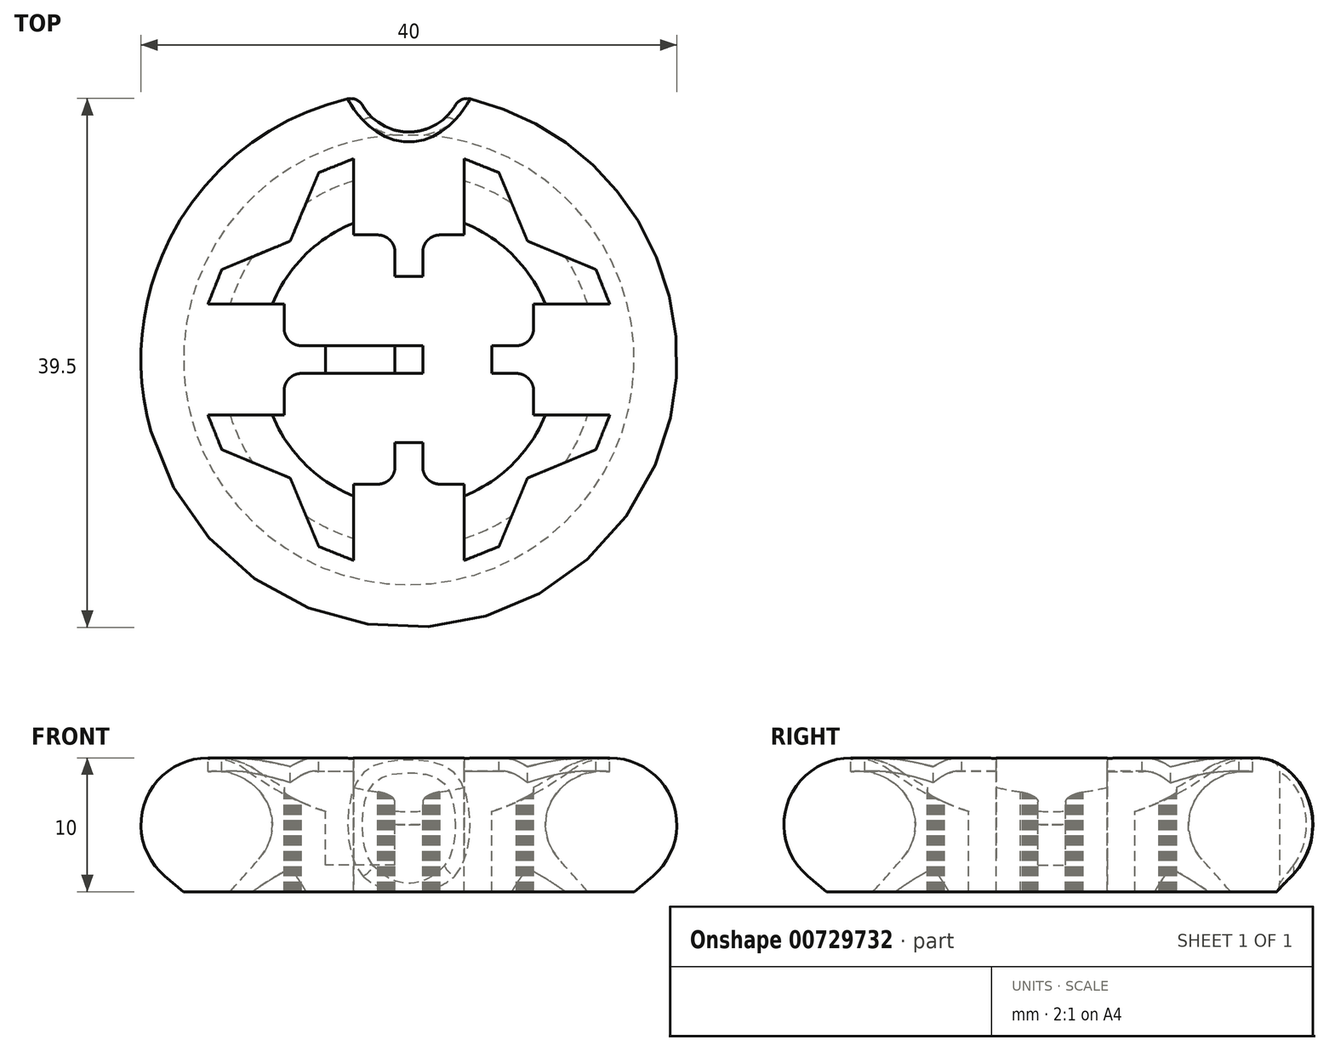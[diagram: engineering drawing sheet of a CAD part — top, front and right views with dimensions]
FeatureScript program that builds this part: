
annotation { "Feature Type Name" : "Feature", "Feature Type Description" : "" }
export const myFeature = defineFeature(function(context is Context, id is Id, definition is map)
    precondition{}
    {
        {
            var Q0;
            Q0=qCreatedBy(makeId("Front.planeOp"),FACE);
            var sketch = newSketch(context, id + "F0", { "sketchPlane" : qUnion([Q0])});
            skArc(sketch, "E0", {"start": v(-12, 9) * mm, "mid": v(-6.32, 6.03) * mm, "end": v(0, 5) * mm});
            skArc(sketch, "E1", {"start": v(-12, 9) * mm, "mid": v(-19.74, 6.58) * mm, "end": v(-15, 0) * mm});
            skLineSegment(sketch, "E2", {"start": v(0, 0) * mm, "end": v(-15, 0) * mm});
            skLineSegment(sketch, "E3", {"start": v(0, 0) * mm, "end": v(0, 5) * mm});
            skLineSegment(sketch, "E4", {"start": v(-18.21, 1.17) * mm, "end": v(-16.82, 0) * mm});
            skLineSegment(sketch, "E5", {"start": v(-16.82, 0) * mm, "end": v(-15, 0) * mm});
            skSolve(sketch);
        }
        {
            var Q0;
            Q0 = qSketchRegion(id + "F0", true);
            var Q1;
            Q1=sQuery(id+"F0.wireOp",EDGE,"E3");
            revolve(context, id + "F1", {"surfaceOperationType" : NewSurfaceOperationType.NEW, "entities" : qUnion([Q0]), "axis" : qUnion([Q1]), "revolveType" : RevolveType.FULL});
        }
        {
            var Q0;
            Q0=qCreatedBy(makeId("Top.planeOp"),FACE);
            cPlane(context, id + "F2", {"entities" : qUnion([Q0]), "cplaneType" : CPlaneType.OFFSET, "offset" : 15 * mm, "width" : 150 * mm, "height" : 150 * mm});
        }
        {
            var Q0;
            Q0=qCreatedBy(id+"F2.planeOp",FACE);
            var sketch = newSketch(context, id + "F3", { "sketchPlane" : qUnion([Q0])});
            skLineSegment(sketch, "E6", {"start": v(9.31, -4.14) * mm, "end": v(9.31, -4.02) * mm});
            skLineSegment(sketch, "E7", {"start": v(9.31, -4.02) * mm, "end": v(9.31, -3.91) * mm});
            skLineSegment(sketch, "E8", {"start": v(9.31, -3.91) * mm, "end": v(9.31, -3.8) * mm});
            skLineSegment(sketch, "E9", {"start": v(9.31, -3.8) * mm, "end": v(9.31, -3.69) * mm});
            skLineSegment(sketch, "E10", {"start": v(9.31, -3.69) * mm, "end": v(9.31, -3.57) * mm});
            skLineSegment(sketch, "E11", {"start": v(9.31, -3.57) * mm, "end": v(9.31, -3.46) * mm});
            skLineSegment(sketch, "E12", {"start": v(9.31, -3.46) * mm, "end": v(9.31, -3.35) * mm});
            skLineSegment(sketch, "E13", {"start": v(9.31, -3.35) * mm, "end": v(9.31, -3.23) * mm});
            skLineSegment(sketch, "E14", {"start": v(9.31, -3.23) * mm, "end": v(9.31, -3.12) * mm});
            skLineSegment(sketch, "E15", {"start": v(9.31, -3.12) * mm, "end": v(9.31, -3) * mm});
            skLineSegment(sketch, "E16", {"start": v(9.31, -3) * mm, "end": v(9.31, -2.9) * mm});
            skLineSegment(sketch, "E17", {"start": v(9.31, -2.9) * mm, "end": v(9.31, -2.78) * mm});
            skLineSegment(sketch, "E18", {"start": v(9.31, -2.78) * mm, "end": v(9.31, -2.67) * mm});
            skLineSegment(sketch, "E19", {"start": v(9.31, -2.67) * mm, "end": v(9.31, -2.55) * mm});
            skLineSegment(sketch, "E20", {"start": v(9.31, -2.55) * mm, "end": v(9.31, -2.44) * mm});
            skLineSegment(sketch, "E21", {"start": v(9.31, -2.44) * mm, "end": v(9.31, -2.33) * mm});
            skLineSegment(sketch, "E22", {"start": v(9.31, -2.33) * mm, "end": v(9.3, -2.2) * mm});
            skLineSegment(sketch, "E23", {"start": v(9.3, -2.2) * mm, "end": v(9.28, -2.07) * mm});
            skLineSegment(sketch, "E24", {"start": v(9.28, -2.07) * mm, "end": v(9.25, -1.94) * mm});
            skLineSegment(sketch, "E25", {"start": v(9.25, -1.94) * mm, "end": v(9.2, -1.82) * mm});
            skLineSegment(sketch, "E26", {"start": v(9.2, -1.82) * mm, "end": v(9.15, -1.71) * mm});
            skLineSegment(sketch, "E27", {"start": v(9.15, -1.71) * mm, "end": v(9.09, -1.6) * mm});
            skLineSegment(sketch, "E28", {"start": v(9.09, -1.6) * mm, "end": v(9.02, -1.5) * mm});
            skLineSegment(sketch, "E29", {"start": v(9.02, -1.5) * mm, "end": v(8.93, -1.41) * mm});
            skLineSegment(sketch, "E30", {"start": v(8.93, -1.41) * mm, "end": v(8.84, -1.33) * mm});
            skLineSegment(sketch, "E31", {"start": v(8.84, -1.33) * mm, "end": v(8.74, -1.26) * mm});
            skLineSegment(sketch, "E32", {"start": v(8.74, -1.26) * mm, "end": v(8.63, -1.2) * mm});
            skLineSegment(sketch, "E33", {"start": v(8.63, -1.2) * mm, "end": v(8.52, -1.14) * mm});
            skLineSegment(sketch, "E34", {"start": v(8.52, -1.14) * mm, "end": v(8.4, -1.1) * mm});
            skLineSegment(sketch, "E35", {"start": v(8.4, -1.1) * mm, "end": v(8.28, -1.06) * mm});
            skLineSegment(sketch, "E36", {"start": v(8.28, -1.06) * mm, "end": v(8.15, -1.04) * mm});
            skLineSegment(sketch, "E37", {"start": v(8.15, -1.04) * mm, "end": v(8.02, -1.03) * mm});
            skLineSegment(sketch, "E38", {"start": v(8.02, -1.03) * mm, "end": v(7.9, -1.03) * mm});
            skLineSegment(sketch, "E39", {"start": v(7.9, -1.03) * mm, "end": v(7.8, -1.03) * mm});
            skLineSegment(sketch, "E40", {"start": v(7.8, -1.03) * mm, "end": v(7.68, -1.03) * mm});
            skLineSegment(sketch, "E41", {"start": v(7.68, -1.03) * mm, "end": v(7.56, -1.03) * mm});
            skLineSegment(sketch, "E42", {"start": v(7.56, -1.03) * mm, "end": v(7.45, -1.03) * mm});
            skLineSegment(sketch, "E43", {"start": v(7.45, -1.03) * mm, "end": v(7.34, -1.03) * mm});
            skLineSegment(sketch, "E44", {"start": v(7.34, -1.03) * mm, "end": v(7.23, -1.03) * mm});
            skLineSegment(sketch, "E45", {"start": v(7.23, -1.03) * mm, "end": v(7.11, -1.03) * mm});
            skLineSegment(sketch, "E46", {"start": v(7.11, -1.03) * mm, "end": v(7, -1.03) * mm});
            skLineSegment(sketch, "E47", {"start": v(7, -1.03) * mm, "end": v(6.89, -1.03) * mm});
            skLineSegment(sketch, "E48", {"start": v(6.89, -1.03) * mm, "end": v(6.77, -1.03) * mm});
            skLineSegment(sketch, "E49", {"start": v(6.77, -1.03) * mm, "end": v(6.66, -1.03) * mm});
            skLineSegment(sketch, "E50", {"start": v(6.66, -1.03) * mm, "end": v(6.55, -1.03) * mm});
            skLineSegment(sketch, "E51", {"start": v(6.55, -1.03) * mm, "end": v(6.43, -1.03) * mm});
            skLineSegment(sketch, "E52", {"start": v(6.43, -1.03) * mm, "end": v(6.32, -1.03) * mm});
            skLineSegment(sketch, "E53", {"start": v(6.32, -1.03) * mm, "end": v(6.2, -1.03) * mm});
            skLineSegment(sketch, "E54", {"start": v(6.2, -1.03) * mm, "end": v(6.2, -0.97) * mm});
            skLineSegment(sketch, "E55", {"start": v(6.2, -0.97) * mm, "end": v(6.2, -0.9) * mm});
            skLineSegment(sketch, "E56", {"start": v(6.2, -0.9) * mm, "end": v(6.2, -0.84) * mm});
            skLineSegment(sketch, "E57", {"start": v(6.2, -0.84) * mm, "end": v(6.2, -0.78) * mm});
            skLineSegment(sketch, "E58", {"start": v(6.2, -0.78) * mm, "end": v(6.2, -0.71) * mm});
            skLineSegment(sketch, "E59", {"start": v(6.2, -0.71) * mm, "end": v(6.2, -0.65) * mm});
            skLineSegment(sketch, "E60", {"start": v(6.2, -0.65) * mm, "end": v(6.2, -0.58) * mm});
            skLineSegment(sketch, "E61", {"start": v(6.2, -0.58) * mm, "end": v(6.2, -0.52) * mm});
            skLineSegment(sketch, "E62", {"start": v(6.2, -0.52) * mm, "end": v(6.2, -0.45) * mm});
            skLineSegment(sketch, "E63", {"start": v(6.2, -0.45) * mm, "end": v(6.2, -0.39) * mm});
            skLineSegment(sketch, "E64", {"start": v(6.2, -0.39) * mm, "end": v(6.2, -0.32) * mm});
            skLineSegment(sketch, "E65", {"start": v(6.2, -0.32) * mm, "end": v(6.2, -0.26) * mm});
            skLineSegment(sketch, "E66", {"start": v(6.2, -0.26) * mm, "end": v(6.2, -0.2) * mm});
            skLineSegment(sketch, "E67", {"start": v(6.2, -0.2) * mm, "end": v(6.2, -0.13) * mm});
            skLineSegment(sketch, "E68", {"start": v(6.2, -0.13) * mm, "end": v(6.2, -0.06) * mm});
            skLineSegment(sketch, "E69", {"start": v(6.2, -0.06) * mm, "end": v(6.2, 0) * mm});
            skLineSegment(sketch, "E70", {"start": v(6.2, 0) * mm, "end": v(6.2, 0.06) * mm});
            skLineSegment(sketch, "E71", {"start": v(6.2, 0.06) * mm, "end": v(6.2, 0.13) * mm});
            skLineSegment(sketch, "E72", {"start": v(6.2, 0.13) * mm, "end": v(6.2, 0.2) * mm});
            skLineSegment(sketch, "E73", {"start": v(6.2, 0.2) * mm, "end": v(6.2, 0.26) * mm});
            skLineSegment(sketch, "E74", {"start": v(6.2, 0.26) * mm, "end": v(6.2, 0.32) * mm});
            skLineSegment(sketch, "E75", {"start": v(6.2, 0.32) * mm, "end": v(6.2, 0.39) * mm});
            skLineSegment(sketch, "E76", {"start": v(6.2, 0.39) * mm, "end": v(6.2, 0.45) * mm});
            skLineSegment(sketch, "E77", {"start": v(6.2, 0.45) * mm, "end": v(6.2, 0.52) * mm});
            skLineSegment(sketch, "E78", {"start": v(6.2, 0.52) * mm, "end": v(6.2, 0.58) * mm});
            skLineSegment(sketch, "E79", {"start": v(6.2, 0.58) * mm, "end": v(6.2, 0.65) * mm});
            skLineSegment(sketch, "E80", {"start": v(6.2, 0.65) * mm, "end": v(6.2, 0.71) * mm});
            skLineSegment(sketch, "E81", {"start": v(6.2, 0.71) * mm, "end": v(6.2, 0.78) * mm});
            skLineSegment(sketch, "E82", {"start": v(6.2, 0.78) * mm, "end": v(6.2, 0.84) * mm});
            skLineSegment(sketch, "E83", {"start": v(6.2, 0.84) * mm, "end": v(6.2, 0.9) * mm});
            skLineSegment(sketch, "E84", {"start": v(6.2, 0.9) * mm, "end": v(6.2, 0.97) * mm});
            skLineSegment(sketch, "E85", {"start": v(6.2, 0.97) * mm, "end": v(6.2, 1.03) * mm});
            skLineSegment(sketch, "E86", {"start": v(6.2, 1.03) * mm, "end": v(6.32, 1.03) * mm});
            skLineSegment(sketch, "E87", {"start": v(6.32, 1.03) * mm, "end": v(6.43, 1.03) * mm});
            skLineSegment(sketch, "E88", {"start": v(6.43, 1.03) * mm, "end": v(6.55, 1.03) * mm});
            skLineSegment(sketch, "E89", {"start": v(6.55, 1.03) * mm, "end": v(6.66, 1.03) * mm});
            skLineSegment(sketch, "E90", {"start": v(6.66, 1.03) * mm, "end": v(6.77, 1.03) * mm});
            skLineSegment(sketch, "E91", {"start": v(6.77, 1.03) * mm, "end": v(6.89, 1.03) * mm});
            skLineSegment(sketch, "E92", {"start": v(6.89, 1.03) * mm, "end": v(7, 1.03) * mm});
            skLineSegment(sketch, "E93", {"start": v(7, 1.03) * mm, "end": v(7.11, 1.03) * mm});
            skLineSegment(sketch, "E94", {"start": v(7.11, 1.03) * mm, "end": v(7.23, 1.03) * mm});
            skLineSegment(sketch, "E95", {"start": v(7.23, 1.03) * mm, "end": v(7.34, 1.03) * mm});
            skLineSegment(sketch, "E96", {"start": v(7.34, 1.03) * mm, "end": v(7.45, 1.03) * mm});
            skLineSegment(sketch, "E97", {"start": v(7.45, 1.03) * mm, "end": v(7.56, 1.03) * mm});
            skLineSegment(sketch, "E98", {"start": v(7.56, 1.03) * mm, "end": v(7.68, 1.03) * mm});
            skLineSegment(sketch, "E99", {"start": v(7.68, 1.03) * mm, "end": v(7.8, 1.03) * mm});
            skLineSegment(sketch, "E100", {"start": v(7.8, 1.03) * mm, "end": v(7.9, 1.03) * mm});
            skLineSegment(sketch, "E101", {"start": v(7.9, 1.03) * mm, "end": v(8.02, 1.03) * mm});
            skLineSegment(sketch, "E102", {"start": v(8.02, 1.03) * mm, "end": v(8.15, 1.04) * mm});
            skLineSegment(sketch, "E103", {"start": v(8.15, 1.04) * mm, "end": v(8.28, 1.06) * mm});
            skLineSegment(sketch, "E104", {"start": v(8.28, 1.06) * mm, "end": v(8.4, 1.1) * mm});
            skLineSegment(sketch, "E105", {"start": v(8.4, 1.1) * mm, "end": v(8.52, 1.14) * mm});
            skLineSegment(sketch, "E106", {"start": v(8.52, 1.14) * mm, "end": v(8.63, 1.2) * mm});
            skLineSegment(sketch, "E107", {"start": v(8.63, 1.2) * mm, "end": v(8.74, 1.26) * mm});
            skLineSegment(sketch, "E108", {"start": v(8.74, 1.26) * mm, "end": v(8.84, 1.33) * mm});
            skLineSegment(sketch, "E109", {"start": v(8.84, 1.33) * mm, "end": v(8.93, 1.41) * mm});
            skLineSegment(sketch, "E110", {"start": v(8.93, 1.41) * mm, "end": v(9.02, 1.5) * mm});
            skLineSegment(sketch, "E111", {"start": v(9.02, 1.5) * mm, "end": v(9.09, 1.6) * mm});
            skLineSegment(sketch, "E112", {"start": v(9.09, 1.6) * mm, "end": v(9.15, 1.71) * mm});
            skLineSegment(sketch, "E113", {"start": v(9.15, 1.71) * mm, "end": v(9.2, 1.82) * mm});
            skLineSegment(sketch, "E114", {"start": v(9.2, 1.82) * mm, "end": v(9.25, 1.94) * mm});
            skLineSegment(sketch, "E115", {"start": v(9.25, 1.94) * mm, "end": v(9.28, 2.07) * mm});
            skLineSegment(sketch, "E116", {"start": v(9.28, 2.07) * mm, "end": v(9.3, 2.2) * mm});
            skLineSegment(sketch, "E117", {"start": v(9.3, 2.2) * mm, "end": v(9.31, 2.33) * mm});
            skLineSegment(sketch, "E118", {"start": v(9.31, 2.33) * mm, "end": v(9.31, 2.44) * mm});
            skLineSegment(sketch, "E119", {"start": v(9.31, 2.44) * mm, "end": v(9.31, 2.55) * mm});
            skLineSegment(sketch, "E120", {"start": v(9.31, 2.55) * mm, "end": v(9.31, 2.67) * mm});
            skLineSegment(sketch, "E121", {"start": v(9.31, 2.67) * mm, "end": v(9.31, 2.78) * mm});
            skLineSegment(sketch, "E122", {"start": v(9.31, 2.78) * mm, "end": v(9.31, 2.9) * mm});
            skLineSegment(sketch, "E123", {"start": v(9.31, 2.9) * mm, "end": v(9.31, 3) * mm});
            skLineSegment(sketch, "E124", {"start": v(9.31, 3) * mm, "end": v(9.31, 3.12) * mm});
            skLineSegment(sketch, "E125", {"start": v(9.31, 3.12) * mm, "end": v(9.31, 3.23) * mm});
            skLineSegment(sketch, "E126", {"start": v(9.31, 3.23) * mm, "end": v(9.31, 3.35) * mm});
            skLineSegment(sketch, "E127", {"start": v(9.31, 3.35) * mm, "end": v(9.31, 3.46) * mm});
            skLineSegment(sketch, "E128", {"start": v(9.31, 3.46) * mm, "end": v(9.31, 3.57) * mm});
            skLineSegment(sketch, "E129", {"start": v(9.31, 3.57) * mm, "end": v(9.31, 3.69) * mm});
            skLineSegment(sketch, "E130", {"start": v(9.31, 3.69) * mm, "end": v(9.31, 3.8) * mm});
            skLineSegment(sketch, "E131", {"start": v(9.31, 3.8) * mm, "end": v(9.31, 3.91) * mm});
            skLineSegment(sketch, "E132", {"start": v(9.31, 3.91) * mm, "end": v(9.31, 4.02) * mm});
            skLineSegment(sketch, "E133", {"start": v(9.31, 4.02) * mm, "end": v(9.31, 4.14) * mm});
            skLineSegment(sketch, "E134", {"start": v(9.31, 4.14) * mm, "end": v(9.44, 4.14) * mm});
            skLineSegment(sketch, "E135", {"start": v(9.44, 4.14) * mm, "end": v(9.57, 4.14) * mm});
            skLineSegment(sketch, "E136", {"start": v(9.57, 4.14) * mm, "end": v(9.7, 4.14) * mm});
            skLineSegment(sketch, "E137", {"start": v(9.7, 4.14) * mm, "end": v(9.83, 4.14) * mm});
            skLineSegment(sketch, "E138", {"start": v(9.83, 4.14) * mm, "end": v(9.96, 4.14) * mm});
            skLineSegment(sketch, "E139", {"start": v(9.96, 4.14) * mm, "end": v(10.09, 4.14) * mm});
            skLineSegment(sketch, "E140", {"start": v(10.09, 4.14) * mm, "end": v(10.22, 4.14) * mm});
            skLineSegment(sketch, "E141", {"start": v(10.22, 4.14) * mm, "end": v(10.34, 4.14) * mm});
            skLineSegment(sketch, "E142", {"start": v(10.34, 4.14) * mm, "end": v(10.47, 4.14) * mm});
            skLineSegment(sketch, "E143", {"start": v(10.47, 4.14) * mm, "end": v(10.6, 4.14) * mm});
            skLineSegment(sketch, "E144", {"start": v(10.6, 4.14) * mm, "end": v(10.73, 4.14) * mm});
            skLineSegment(sketch, "E145", {"start": v(10.73, 4.14) * mm, "end": v(10.86, 4.14) * mm});
            skLineSegment(sketch, "E146", {"start": v(10.86, 4.14) * mm, "end": v(11, 4.14) * mm});
            skLineSegment(sketch, "E147", {"start": v(11, 4.14) * mm, "end": v(11.12, 4.14) * mm});
            skLineSegment(sketch, "E148", {"start": v(11.12, 4.14) * mm, "end": v(11.25, 4.14) * mm});
            skLineSegment(sketch, "E149", {"start": v(11.25, 4.14) * mm, "end": v(11.38, 4.14) * mm});
            skLineSegment(sketch, "E150", {"start": v(11.38, 4.14) * mm, "end": v(11.6, 4.14) * mm});
            skLineSegment(sketch, "E151", {"start": v(11.6, 4.14) * mm, "end": v(11.83, 4.14) * mm});
            skLineSegment(sketch, "E152", {"start": v(11.83, 4.14) * mm, "end": v(12.06, 4.14) * mm});
            skLineSegment(sketch, "E153", {"start": v(12.06, 4.14) * mm, "end": v(12.28, 4.14) * mm});
            skLineSegment(sketch, "E154", {"start": v(12.28, 4.14) * mm, "end": v(12.51, 4.14) * mm});
            skLineSegment(sketch, "E155", {"start": v(12.51, 4.14) * mm, "end": v(12.74, 4.14) * mm});
            skLineSegment(sketch, "E156", {"start": v(12.74, 4.14) * mm, "end": v(12.96, 4.14) * mm});
            skLineSegment(sketch, "E157", {"start": v(12.96, 4.14) * mm, "end": v(13.19, 4.14) * mm});
            skLineSegment(sketch, "E158", {"start": v(13.19, 4.14) * mm, "end": v(13.42, 4.14) * mm});
            skLineSegment(sketch, "E159", {"start": v(13.42, 4.14) * mm, "end": v(13.64, 4.14) * mm});
            skLineSegment(sketch, "E160", {"start": v(13.64, 4.14) * mm, "end": v(13.87, 4.14) * mm});
            skLineSegment(sketch, "E161", {"start": v(13.87, 4.14) * mm, "end": v(14.1, 4.14) * mm});
            skLineSegment(sketch, "E162", {"start": v(14.1, 4.14) * mm, "end": v(14.32, 4.14) * mm});
            skLineSegment(sketch, "E163", {"start": v(14.32, 4.14) * mm, "end": v(14.55, 4.14) * mm});
            skLineSegment(sketch, "E164", {"start": v(14.55, 4.14) * mm, "end": v(14.77, 4.14) * mm});
            skLineSegment(sketch, "E165", {"start": v(14.77, 4.14) * mm, "end": v(15, 4.14) * mm});
            skLineSegment(sketch, "E166", {"start": v(15, 4.14) * mm, "end": v(14.95, 4.27) * mm});
            skLineSegment(sketch, "E167", {"start": v(14.95, 4.27) * mm, "end": v(14.9, 4.4) * mm});
            skLineSegment(sketch, "E168", {"start": v(14.9, 4.4) * mm, "end": v(14.84, 4.53) * mm});
            skLineSegment(sketch, "E169", {"start": v(14.84, 4.53) * mm, "end": v(14.8, 4.66) * mm});
            skLineSegment(sketch, "E170", {"start": v(14.8, 4.66) * mm, "end": v(14.74, 4.78) * mm});
            skLineSegment(sketch, "E171", {"start": v(14.74, 4.78) * mm, "end": v(14.69, 4.91) * mm});
            skLineSegment(sketch, "E172", {"start": v(14.69, 4.91) * mm, "end": v(14.64, 5.04) * mm});
            skLineSegment(sketch, "E173", {"start": v(14.64, 5.04) * mm, "end": v(14.59, 5.17) * mm});
            skLineSegment(sketch, "E174", {"start": v(14.59, 5.17) * mm, "end": v(14.53, 5.3) * mm});
            skLineSegment(sketch, "E175", {"start": v(14.53, 5.3) * mm, "end": v(14.48, 5.43) * mm});
            skLineSegment(sketch, "E176", {"start": v(14.48, 5.43) * mm, "end": v(14.43, 5.56) * mm});
            skLineSegment(sketch, "E177", {"start": v(14.43, 5.56) * mm, "end": v(14.38, 5.69) * mm});
            skLineSegment(sketch, "E178", {"start": v(14.38, 5.69) * mm, "end": v(14.33, 5.82) * mm});
            skLineSegment(sketch, "E179", {"start": v(14.33, 5.82) * mm, "end": v(14.28, 5.95) * mm});
            skLineSegment(sketch, "E180", {"start": v(14.28, 5.95) * mm, "end": v(14.22, 6.08) * mm});
            skLineSegment(sketch, "E181", {"start": v(14.22, 6.08) * mm, "end": v(14.17, 6.2) * mm});
            skLineSegment(sketch, "E182", {"start": v(14.17, 6.2) * mm, "end": v(14.16, 6.24) * mm});
            skLineSegment(sketch, "E183", {"start": v(14.16, 6.24) * mm, "end": v(14.15, 6.27) * mm});
            skLineSegment(sketch, "E184", {"start": v(14.15, 6.27) * mm, "end": v(14.13, 6.3) * mm});
            skLineSegment(sketch, "E185", {"start": v(14.13, 6.3) * mm, "end": v(14.12, 6.34) * mm});
            skLineSegment(sketch, "E186", {"start": v(14.12, 6.34) * mm, "end": v(14.1, 6.37) * mm});
            skLineSegment(sketch, "E187", {"start": v(14.1, 6.37) * mm, "end": v(14.1, 6.4) * mm});
            skLineSegment(sketch, "E188", {"start": v(14.1, 6.4) * mm, "end": v(14.08, 6.43) * mm});
            skLineSegment(sketch, "E189", {"start": v(14.08, 6.43) * mm, "end": v(14.07, 6.47) * mm});
            skLineSegment(sketch, "E190", {"start": v(14.07, 6.47) * mm, "end": v(14.06, 6.5) * mm});
            skLineSegment(sketch, "E191", {"start": v(14.06, 6.5) * mm, "end": v(14.04, 6.53) * mm});
            skLineSegment(sketch, "E192", {"start": v(14.04, 6.53) * mm, "end": v(14.03, 6.56) * mm});
            skLineSegment(sketch, "E193", {"start": v(14.03, 6.56) * mm, "end": v(14.02, 6.6) * mm});
            skLineSegment(sketch, "E194", {"start": v(14.02, 6.6) * mm, "end": v(14, 6.63) * mm});
            skLineSegment(sketch, "E195", {"start": v(14, 6.63) * mm, "end": v(14, 6.66) * mm});
            skLineSegment(sketch, "E196", {"start": v(14, 6.66) * mm, "end": v(13.98, 6.7) * mm});
            skLineSegment(sketch, "E197", {"start": v(13.98, 6.7) * mm, "end": v(13.97, 6.72) * mm});
            skLineSegment(sketch, "E198", {"start": v(13.97, 6.72) * mm, "end": v(13.65, 6.86) * mm});
            skLineSegment(sketch, "E199", {"start": v(13.65, 6.86) * mm, "end": v(13.33, 7) * mm});
            skLineSegment(sketch, "E200", {"start": v(13.33, 7) * mm, "end": v(13, 7.12) * mm});
            skLineSegment(sketch, "E201", {"start": v(13, 7.12) * mm, "end": v(12.69, 7.26) * mm});
            skLineSegment(sketch, "E202", {"start": v(12.69, 7.26) * mm, "end": v(12.37, 7.39) * mm});
            skLineSegment(sketch, "E203", {"start": v(12.37, 7.39) * mm, "end": v(12.05, 7.52) * mm});
            skLineSegment(sketch, "E204", {"start": v(12.05, 7.52) * mm, "end": v(11.73, 7.66) * mm});
            skLineSegment(sketch, "E205", {"start": v(11.73, 7.66) * mm, "end": v(11.4, 7.79) * mm});
            skLineSegment(sketch, "E206", {"start": v(11.4, 7.79) * mm, "end": v(11.1, 7.92) * mm});
            skLineSegment(sketch, "E207", {"start": v(11.1, 7.92) * mm, "end": v(10.77, 8.06) * mm});
            skLineSegment(sketch, "E208", {"start": v(10.77, 8.06) * mm, "end": v(10.45, 8.19) * mm});
            skLineSegment(sketch, "E209", {"start": v(10.45, 8.19) * mm, "end": v(10.13, 8.32) * mm});
            skLineSegment(sketch, "E210", {"start": v(10.13, 8.32) * mm, "end": v(9.81, 8.45) * mm});
            skLineSegment(sketch, "E211", {"start": v(9.81, 8.45) * mm, "end": v(9.5, 8.59) * mm});
            skLineSegment(sketch, "E212", {"start": v(9.5, 8.59) * mm, "end": v(9.17, 8.72) * mm});
            skLineSegment(sketch, "E213", {"start": v(9.17, 8.72) * mm, "end": v(8.85, 8.85) * mm});
            skLineSegment(sketch, "E214", {"start": v(8.85, 8.85) * mm, "end": v(8.72, 9.17) * mm});
            skLineSegment(sketch, "E215", {"start": v(8.72, 9.17) * mm, "end": v(8.59, 9.5) * mm});
            skLineSegment(sketch, "E216", {"start": v(8.59, 9.5) * mm, "end": v(8.45, 9.81) * mm});
            skLineSegment(sketch, "E217", {"start": v(8.45, 9.81) * mm, "end": v(8.32, 10.13) * mm});
            skLineSegment(sketch, "E218", {"start": v(8.32, 10.13) * mm, "end": v(8.19, 10.45) * mm});
            skLineSegment(sketch, "E219", {"start": v(8.19, 10.45) * mm, "end": v(8.06, 10.77) * mm});
            skLineSegment(sketch, "E220", {"start": v(8.06, 10.77) * mm, "end": v(7.92, 11.1) * mm});
            skLineSegment(sketch, "E221", {"start": v(7.92, 11.1) * mm, "end": v(7.79, 11.4) * mm});
            skLineSegment(sketch, "E222", {"start": v(7.79, 11.4) * mm, "end": v(7.66, 11.73) * mm});
            skLineSegment(sketch, "E223", {"start": v(7.66, 11.73) * mm, "end": v(7.52, 12.05) * mm});
            skLineSegment(sketch, "E224", {"start": v(7.52, 12.05) * mm, "end": v(7.39, 12.37) * mm});
            skLineSegment(sketch, "E225", {"start": v(7.39, 12.37) * mm, "end": v(7.26, 12.69) * mm});
            skLineSegment(sketch, "E226", {"start": v(7.26, 12.69) * mm, "end": v(7.12, 13) * mm});
            skLineSegment(sketch, "E227", {"start": v(7.12, 13) * mm, "end": v(7, 13.33) * mm});
            skLineSegment(sketch, "E228", {"start": v(7, 13.33) * mm, "end": v(6.86, 13.65) * mm});
            skLineSegment(sketch, "E229", {"start": v(6.86, 13.65) * mm, "end": v(6.72, 13.97) * mm});
            skLineSegment(sketch, "E230", {"start": v(6.72, 13.97) * mm, "end": v(6.7, 13.98) * mm});
            skLineSegment(sketch, "E231", {"start": v(6.7, 13.98) * mm, "end": v(6.66, 14) * mm});
            skLineSegment(sketch, "E232", {"start": v(6.66, 14) * mm, "end": v(6.63, 14) * mm});
            skLineSegment(sketch, "E233", {"start": v(6.63, 14) * mm, "end": v(6.6, 14.02) * mm});
            skLineSegment(sketch, "E234", {"start": v(6.6, 14.02) * mm, "end": v(6.56, 14.03) * mm});
            skLineSegment(sketch, "E235", {"start": v(6.56, 14.03) * mm, "end": v(6.53, 14.04) * mm});
            skLineSegment(sketch, "E236", {"start": v(6.53, 14.04) * mm, "end": v(6.5, 14.06) * mm});
            skLineSegment(sketch, "E237", {"start": v(6.5, 14.06) * mm, "end": v(6.47, 14.07) * mm});
            skLineSegment(sketch, "E238", {"start": v(6.47, 14.07) * mm, "end": v(6.43, 14.08) * mm});
            skLineSegment(sketch, "E239", {"start": v(6.43, 14.08) * mm, "end": v(6.4, 14.1) * mm});
            skLineSegment(sketch, "E240", {"start": v(6.4, 14.1) * mm, "end": v(6.37, 14.1) * mm});
            skLineSegment(sketch, "E241", {"start": v(6.37, 14.1) * mm, "end": v(6.34, 14.12) * mm});
            skLineSegment(sketch, "E242", {"start": v(6.34, 14.12) * mm, "end": v(6.3, 14.13) * mm});
            skLineSegment(sketch, "E243", {"start": v(6.3, 14.13) * mm, "end": v(6.27, 14.15) * mm});
            skLineSegment(sketch, "E244", {"start": v(6.27, 14.15) * mm, "end": v(6.24, 14.16) * mm});
            skLineSegment(sketch, "E245", {"start": v(6.24, 14.16) * mm, "end": v(6.2, 14.17) * mm});
            skLineSegment(sketch, "E246", {"start": v(6.2, 14.17) * mm, "end": v(6.08, 14.22) * mm});
            skLineSegment(sketch, "E247", {"start": v(6.08, 14.22) * mm, "end": v(5.95, 14.28) * mm});
            skLineSegment(sketch, "E248", {"start": v(5.95, 14.28) * mm, "end": v(5.82, 14.33) * mm});
            skLineSegment(sketch, "E249", {"start": v(5.82, 14.33) * mm, "end": v(5.69, 14.38) * mm});
            skLineSegment(sketch, "E250", {"start": v(5.69, 14.38) * mm, "end": v(5.56, 14.43) * mm});
            skLineSegment(sketch, "E251", {"start": v(5.56, 14.43) * mm, "end": v(5.43, 14.48) * mm});
            skLineSegment(sketch, "E252", {"start": v(5.43, 14.48) * mm, "end": v(5.3, 14.53) * mm});
            skLineSegment(sketch, "E253", {"start": v(5.3, 14.53) * mm, "end": v(5.17, 14.59) * mm});
            skLineSegment(sketch, "E254", {"start": v(5.17, 14.59) * mm, "end": v(5.04, 14.64) * mm});
            skLineSegment(sketch, "E255", {"start": v(5.04, 14.64) * mm, "end": v(4.91, 14.69) * mm});
            skLineSegment(sketch, "E256", {"start": v(4.91, 14.69) * mm, "end": v(4.78, 14.74) * mm});
            skLineSegment(sketch, "E257", {"start": v(4.78, 14.74) * mm, "end": v(4.66, 14.8) * mm});
            skLineSegment(sketch, "E258", {"start": v(4.66, 14.8) * mm, "end": v(4.53, 14.84) * mm});
            skLineSegment(sketch, "E259", {"start": v(4.53, 14.84) * mm, "end": v(4.4, 14.9) * mm});
            skLineSegment(sketch, "E260", {"start": v(4.4, 14.9) * mm, "end": v(4.27, 14.95) * mm});
            skLineSegment(sketch, "E261", {"start": v(4.27, 14.95) * mm, "end": v(4.14, 15) * mm});
            skLineSegment(sketch, "E262", {"start": v(4.14, 15) * mm, "end": v(4.14, 14.77) * mm});
            skLineSegment(sketch, "E263", {"start": v(4.14, 14.77) * mm, "end": v(4.14, 14.55) * mm});
            skLineSegment(sketch, "E264", {"start": v(4.14, 14.55) * mm, "end": v(4.14, 14.32) * mm});
            skLineSegment(sketch, "E265", {"start": v(4.14, 14.32) * mm, "end": v(4.14, 14.1) * mm});
            skLineSegment(sketch, "E266", {"start": v(4.14, 14.1) * mm, "end": v(4.14, 13.87) * mm});
            skLineSegment(sketch, "E267", {"start": v(4.14, 13.87) * mm, "end": v(4.14, 13.64) * mm});
            skLineSegment(sketch, "E268", {"start": v(4.14, 13.64) * mm, "end": v(4.14, 13.42) * mm});
            skLineSegment(sketch, "E269", {"start": v(4.14, 13.42) * mm, "end": v(4.14, 13.19) * mm});
            skLineSegment(sketch, "E270", {"start": v(4.14, 13.19) * mm, "end": v(4.14, 12.96) * mm});
            skLineSegment(sketch, "E271", {"start": v(4.14, 12.96) * mm, "end": v(4.14, 12.74) * mm});
            skLineSegment(sketch, "E272", {"start": v(4.14, 12.74) * mm, "end": v(4.14, 12.51) * mm});
            skLineSegment(sketch, "E273", {"start": v(4.14, 12.51) * mm, "end": v(4.14, 12.28) * mm});
            skLineSegment(sketch, "E274", {"start": v(4.14, 12.28) * mm, "end": v(4.14, 12.06) * mm});
            skLineSegment(sketch, "E275", {"start": v(4.14, 12.06) * mm, "end": v(4.14, 11.83) * mm});
            skLineSegment(sketch, "E276", {"start": v(4.14, 11.83) * mm, "end": v(4.14, 11.6) * mm});
            skLineSegment(sketch, "E277", {"start": v(4.14, 11.6) * mm, "end": v(4.14, 11.38) * mm});
            skLineSegment(sketch, "E278", {"start": v(4.14, 11.38) * mm, "end": v(4.14, 11.25) * mm});
            skLineSegment(sketch, "E279", {"start": v(4.14, 11.25) * mm, "end": v(4.14, 11.12) * mm});
            skLineSegment(sketch, "E280", {"start": v(4.14, 11.12) * mm, "end": v(4.14, 11) * mm});
            skLineSegment(sketch, "E281", {"start": v(4.14, 11) * mm, "end": v(4.14, 10.86) * mm});
            skLineSegment(sketch, "E282", {"start": v(4.14, 10.86) * mm, "end": v(4.14, 10.73) * mm});
            skLineSegment(sketch, "E283", {"start": v(4.14, 10.73) * mm, "end": v(4.14, 10.6) * mm});
            skLineSegment(sketch, "E284", {"start": v(4.14, 10.6) * mm, "end": v(4.14, 10.47) * mm});
            skLineSegment(sketch, "E285", {"start": v(4.14, 10.47) * mm, "end": v(4.14, 10.34) * mm});
            skLineSegment(sketch, "E286", {"start": v(4.14, 10.34) * mm, "end": v(4.14, 10.22) * mm});
            skLineSegment(sketch, "E287", {"start": v(4.14, 10.22) * mm, "end": v(4.14, 10.09) * mm});
            skLineSegment(sketch, "E288", {"start": v(4.14, 10.09) * mm, "end": v(4.14, 9.96) * mm});
            skLineSegment(sketch, "E289", {"start": v(4.14, 9.96) * mm, "end": v(4.14, 9.83) * mm});
            skLineSegment(sketch, "E290", {"start": v(4.14, 9.83) * mm, "end": v(4.14, 9.7) * mm});
            skLineSegment(sketch, "E291", {"start": v(4.14, 9.7) * mm, "end": v(4.14, 9.57) * mm});
            skLineSegment(sketch, "E292", {"start": v(4.14, 9.57) * mm, "end": v(4.14, 9.44) * mm});
            skLineSegment(sketch, "E293", {"start": v(4.14, 9.44) * mm, "end": v(4.14, 9.31) * mm});
            skLineSegment(sketch, "E294", {"start": v(4.14, 9.31) * mm, "end": v(4.02, 9.31) * mm});
            skLineSegment(sketch, "E295", {"start": v(4.02, 9.31) * mm, "end": v(3.91, 9.31) * mm});
            skLineSegment(sketch, "E296", {"start": v(3.91, 9.31) * mm, "end": v(3.8, 9.31) * mm});
            skLineSegment(sketch, "E297", {"start": v(3.8, 9.31) * mm, "end": v(3.69, 9.31) * mm});
            skLineSegment(sketch, "E298", {"start": v(3.69, 9.31) * mm, "end": v(3.57, 9.31) * mm});
            skLineSegment(sketch, "E299", {"start": v(3.57, 9.31) * mm, "end": v(3.46, 9.31) * mm});
            skLineSegment(sketch, "E300", {"start": v(3.46, 9.31) * mm, "end": v(3.35, 9.31) * mm});
            skLineSegment(sketch, "E301", {"start": v(3.35, 9.31) * mm, "end": v(3.23, 9.31) * mm});
            skLineSegment(sketch, "E302", {"start": v(3.23, 9.31) * mm, "end": v(3.12, 9.31) * mm});
            skLineSegment(sketch, "E303", {"start": v(3.12, 9.31) * mm, "end": v(3, 9.31) * mm});
            skLineSegment(sketch, "E304", {"start": v(3, 9.31) * mm, "end": v(2.9, 9.31) * mm});
            skLineSegment(sketch, "E305", {"start": v(2.9, 9.31) * mm, "end": v(2.78, 9.31) * mm});
            skLineSegment(sketch, "E306", {"start": v(2.78, 9.31) * mm, "end": v(2.67, 9.31) * mm});
            skLineSegment(sketch, "E307", {"start": v(2.67, 9.31) * mm, "end": v(2.55, 9.31) * mm});
            skLineSegment(sketch, "E308", {"start": v(2.55, 9.31) * mm, "end": v(2.44, 9.31) * mm});
            skLineSegment(sketch, "E309", {"start": v(2.44, 9.31) * mm, "end": v(2.33, 9.31) * mm});
            skLineSegment(sketch, "E310", {"start": v(2.33, 9.31) * mm, "end": v(2.2, 9.3) * mm});
            skLineSegment(sketch, "E311", {"start": v(2.2, 9.3) * mm, "end": v(2.07, 9.28) * mm});
            skLineSegment(sketch, "E312", {"start": v(2.07, 9.28) * mm, "end": v(1.94, 9.25) * mm});
            skLineSegment(sketch, "E313", {"start": v(1.94, 9.25) * mm, "end": v(1.82, 9.2) * mm});
            skLineSegment(sketch, "E314", {"start": v(1.82, 9.2) * mm, "end": v(1.71, 9.15) * mm});
            skLineSegment(sketch, "E315", {"start": v(1.71, 9.15) * mm, "end": v(1.6, 9.09) * mm});
            skLineSegment(sketch, "E316", {"start": v(1.6, 9.09) * mm, "end": v(1.5, 9.02) * mm});
            skLineSegment(sketch, "E317", {"start": v(1.5, 9.02) * mm, "end": v(1.41, 8.93) * mm});
            skLineSegment(sketch, "E318", {"start": v(1.41, 8.93) * mm, "end": v(1.33, 8.84) * mm});
            skLineSegment(sketch, "E319", {"start": v(1.33, 8.84) * mm, "end": v(1.26, 8.74) * mm});
            skLineSegment(sketch, "E320", {"start": v(1.26, 8.74) * mm, "end": v(1.2, 8.63) * mm});
            skLineSegment(sketch, "E321", {"start": v(1.2, 8.63) * mm, "end": v(1.14, 8.52) * mm});
            skLineSegment(sketch, "E322", {"start": v(1.14, 8.52) * mm, "end": v(1.1, 8.4) * mm});
            skLineSegment(sketch, "E323", {"start": v(1.1, 8.4) * mm, "end": v(1.06, 8.28) * mm});
            skLineSegment(sketch, "E324", {"start": v(1.06, 8.28) * mm, "end": v(1.04, 8.15) * mm});
            skLineSegment(sketch, "E325", {"start": v(1.04, 8.15) * mm, "end": v(1.03, 8.02) * mm});
            skLineSegment(sketch, "E326", {"start": v(1.03, 8.02) * mm, "end": v(1.03, 7.9) * mm});
            skLineSegment(sketch, "E327", {"start": v(1.03, 7.9) * mm, "end": v(1.03, 7.8) * mm});
            skLineSegment(sketch, "E328", {"start": v(1.03, 7.8) * mm, "end": v(1.03, 7.68) * mm});
            skLineSegment(sketch, "E329", {"start": v(1.03, 7.68) * mm, "end": v(1.03, 7.56) * mm});
            skLineSegment(sketch, "E330", {"start": v(1.03, 7.56) * mm, "end": v(1.03, 7.45) * mm});
            skLineSegment(sketch, "E331", {"start": v(1.03, 7.45) * mm, "end": v(1.03, 7.34) * mm});
            skLineSegment(sketch, "E332", {"start": v(1.03, 7.34) * mm, "end": v(1.03, 7.23) * mm});
            skLineSegment(sketch, "E333", {"start": v(1.03, 7.23) * mm, "end": v(1.03, 7.11) * mm});
            skLineSegment(sketch, "E334", {"start": v(1.03, 7.11) * mm, "end": v(1.03, 7) * mm});
            skLineSegment(sketch, "E335", {"start": v(1.03, 7) * mm, "end": v(1.03, 6.89) * mm});
            skLineSegment(sketch, "E336", {"start": v(1.03, 6.89) * mm, "end": v(1.03, 6.77) * mm});
            skLineSegment(sketch, "E337", {"start": v(1.03, 6.77) * mm, "end": v(1.03, 6.66) * mm});
            skLineSegment(sketch, "E338", {"start": v(1.03, 6.66) * mm, "end": v(1.03, 6.55) * mm});
            skLineSegment(sketch, "E339", {"start": v(1.03, 6.55) * mm, "end": v(1.03, 6.43) * mm});
            skLineSegment(sketch, "E340", {"start": v(1.03, 6.43) * mm, "end": v(1.03, 6.32) * mm});
            skLineSegment(sketch, "E341", {"start": v(1.03, 6.32) * mm, "end": v(1.03, 6.2) * mm});
            skLineSegment(sketch, "E342", {"start": v(1.03, 6.2) * mm, "end": v(0.97, 6.2) * mm});
            skLineSegment(sketch, "E343", {"start": v(0.97, 6.2) * mm, "end": v(0.9, 6.2) * mm});
            skLineSegment(sketch, "E344", {"start": v(0.9, 6.2) * mm, "end": v(0.84, 6.2) * mm});
            skLineSegment(sketch, "E345", {"start": v(0.84, 6.2) * mm, "end": v(0.78, 6.2) * mm});
            skLineSegment(sketch, "E346", {"start": v(0.78, 6.2) * mm, "end": v(0.71, 6.2) * mm});
            skLineSegment(sketch, "E347", {"start": v(0.71, 6.2) * mm, "end": v(0.65, 6.2) * mm});
            skLineSegment(sketch, "E348", {"start": v(0.65, 6.2) * mm, "end": v(0.58, 6.2) * mm});
            skLineSegment(sketch, "E349", {"start": v(0.58, 6.2) * mm, "end": v(0.52, 6.2) * mm});
            skLineSegment(sketch, "E350", {"start": v(0.52, 6.2) * mm, "end": v(0.45, 6.2) * mm});
            skLineSegment(sketch, "E351", {"start": v(0.45, 6.2) * mm, "end": v(0.39, 6.2) * mm});
            skLineSegment(sketch, "E352", {"start": v(0.39, 6.2) * mm, "end": v(0.32, 6.2) * mm});
            skLineSegment(sketch, "E353", {"start": v(0.32, 6.2) * mm, "end": v(0.26, 6.2) * mm});
            skLineSegment(sketch, "E354", {"start": v(0.26, 6.2) * mm, "end": v(0.2, 6.2) * mm});
            skLineSegment(sketch, "E355", {"start": v(0.2, 6.2) * mm, "end": v(0.13, 6.2) * mm});
            skLineSegment(sketch, "E356", {"start": v(0.13, 6.2) * mm, "end": v(0.06, 6.2) * mm});
            skLineSegment(sketch, "E357", {"start": v(0.06, 6.2) * mm, "end": v(0, 6.2) * mm});
            skLineSegment(sketch, "E358", {"start": v(0, 6.2) * mm, "end": v(-0.06, 6.2) * mm});
            skLineSegment(sketch, "E359", {"start": v(-0.06, 6.2) * mm, "end": v(-0.13, 6.2) * mm});
            skLineSegment(sketch, "E360", {"start": v(-0.13, 6.2) * mm, "end": v(-0.2, 6.2) * mm});
            skLineSegment(sketch, "E361", {"start": v(-0.2, 6.2) * mm, "end": v(-0.26, 6.2) * mm});
            skLineSegment(sketch, "E362", {"start": v(-0.26, 6.2) * mm, "end": v(-0.32, 6.2) * mm});
            skLineSegment(sketch, "E363", {"start": v(-0.32, 6.2) * mm, "end": v(-0.39, 6.2) * mm});
            skLineSegment(sketch, "E364", {"start": v(-0.39, 6.2) * mm, "end": v(-0.45, 6.2) * mm});
            skLineSegment(sketch, "E365", {"start": v(-0.45, 6.2) * mm, "end": v(-0.52, 6.2) * mm});
            skLineSegment(sketch, "E366", {"start": v(-0.52, 6.2) * mm, "end": v(-0.58, 6.2) * mm});
            skLineSegment(sketch, "E367", {"start": v(-0.58, 6.2) * mm, "end": v(-0.65, 6.2) * mm});
            skLineSegment(sketch, "E368", {"start": v(-0.65, 6.2) * mm, "end": v(-0.71, 6.2) * mm});
            skLineSegment(sketch, "E369", {"start": v(-0.71, 6.2) * mm, "end": v(-0.78, 6.2) * mm});
            skLineSegment(sketch, "E370", {"start": v(-0.78, 6.2) * mm, "end": v(-0.84, 6.2) * mm});
            skLineSegment(sketch, "E371", {"start": v(-0.84, 6.2) * mm, "end": v(-0.9, 6.2) * mm});
            skLineSegment(sketch, "E372", {"start": v(-0.9, 6.2) * mm, "end": v(-0.97, 6.2) * mm});
            skLineSegment(sketch, "E373", {"start": v(-0.97, 6.2) * mm, "end": v(-1.03, 6.2) * mm});
            skLineSegment(sketch, "E374", {"start": v(-1.03, 6.2) * mm, "end": v(-1.03, 6.32) * mm});
            skLineSegment(sketch, "E375", {"start": v(-1.03, 6.32) * mm, "end": v(-1.03, 6.43) * mm});
            skLineSegment(sketch, "E376", {"start": v(-1.03, 6.43) * mm, "end": v(-1.03, 6.55) * mm});
            skLineSegment(sketch, "E377", {"start": v(-1.03, 6.55) * mm, "end": v(-1.03, 6.66) * mm});
            skLineSegment(sketch, "E378", {"start": v(-1.03, 6.66) * mm, "end": v(-1.03, 6.77) * mm});
            skLineSegment(sketch, "E379", {"start": v(-1.03, 6.77) * mm, "end": v(-1.03, 6.89) * mm});
            skLineSegment(sketch, "E380", {"start": v(-1.03, 6.89) * mm, "end": v(-1.03, 7) * mm});
            skLineSegment(sketch, "E381", {"start": v(-1.03, 7) * mm, "end": v(-1.03, 7.11) * mm});
            skLineSegment(sketch, "E382", {"start": v(-1.03, 7.11) * mm, "end": v(-1.03, 7.23) * mm});
            skLineSegment(sketch, "E383", {"start": v(-1.03, 7.23) * mm, "end": v(-1.03, 7.34) * mm});
            skLineSegment(sketch, "E384", {"start": v(-1.03, 7.34) * mm, "end": v(-1.03, 7.45) * mm});
            skLineSegment(sketch, "E385", {"start": v(-1.03, 7.45) * mm, "end": v(-1.03, 7.56) * mm});
            skLineSegment(sketch, "E386", {"start": v(-1.03, 7.56) * mm, "end": v(-1.03, 7.68) * mm});
            skLineSegment(sketch, "E387", {"start": v(-1.03, 7.68) * mm, "end": v(-1.03, 7.8) * mm});
            skLineSegment(sketch, "E388", {"start": v(-1.03, 7.8) * mm, "end": v(-1.03, 7.9) * mm});
            skLineSegment(sketch, "E389", {"start": v(-1.03, 7.9) * mm, "end": v(-1.03, 8.02) * mm});
            skLineSegment(sketch, "E390", {"start": v(-1.03, 8.02) * mm, "end": v(-1.04, 8.15) * mm});
            skLineSegment(sketch, "E391", {"start": v(-1.04, 8.15) * mm, "end": v(-1.06, 8.28) * mm});
            skLineSegment(sketch, "E392", {"start": v(-1.06, 8.28) * mm, "end": v(-1.1, 8.4) * mm});
            skLineSegment(sketch, "E393", {"start": v(-1.1, 8.4) * mm, "end": v(-1.14, 8.52) * mm});
            skLineSegment(sketch, "E394", {"start": v(-1.14, 8.52) * mm, "end": v(-1.2, 8.63) * mm});
            skLineSegment(sketch, "E395", {"start": v(-1.2, 8.63) * mm, "end": v(-1.26, 8.74) * mm});
            skLineSegment(sketch, "E396", {"start": v(-1.26, 8.74) * mm, "end": v(-1.33, 8.84) * mm});
            skLineSegment(sketch, "E397", {"start": v(-1.33, 8.84) * mm, "end": v(-1.41, 8.93) * mm});
            skLineSegment(sketch, "E398", {"start": v(-1.41, 8.93) * mm, "end": v(-1.5, 9.02) * mm});
            skLineSegment(sketch, "E399", {"start": v(-1.5, 9.02) * mm, "end": v(-1.6, 9.09) * mm});
            skLineSegment(sketch, "E400", {"start": v(-1.6, 9.09) * mm, "end": v(-1.71, 9.15) * mm});
            skLineSegment(sketch, "E401", {"start": v(-1.71, 9.15) * mm, "end": v(-1.82, 9.2) * mm});
            skLineSegment(sketch, "E402", {"start": v(-1.82, 9.2) * mm, "end": v(-1.94, 9.25) * mm});
            skLineSegment(sketch, "E403", {"start": v(-1.94, 9.25) * mm, "end": v(-2.07, 9.28) * mm});
            skLineSegment(sketch, "E404", {"start": v(-2.07, 9.28) * mm, "end": v(-2.2, 9.3) * mm});
            skLineSegment(sketch, "E405", {"start": v(-2.2, 9.3) * mm, "end": v(-2.33, 9.31) * mm});
            skLineSegment(sketch, "E406", {"start": v(-2.33, 9.31) * mm, "end": v(-2.44, 9.31) * mm});
            skLineSegment(sketch, "E407", {"start": v(-2.44, 9.31) * mm, "end": v(-2.55, 9.31) * mm});
            skLineSegment(sketch, "E408", {"start": v(-2.55, 9.31) * mm, "end": v(-2.67, 9.31) * mm});
            skLineSegment(sketch, "E409", {"start": v(-2.67, 9.31) * mm, "end": v(-2.78, 9.31) * mm});
            skLineSegment(sketch, "E410", {"start": v(-2.78, 9.31) * mm, "end": v(-2.9, 9.31) * mm});
            skLineSegment(sketch, "E411", {"start": v(-2.9, 9.31) * mm, "end": v(-3, 9.31) * mm});
            skLineSegment(sketch, "E412", {"start": v(-3, 9.31) * mm, "end": v(-3.12, 9.31) * mm});
            skLineSegment(sketch, "E413", {"start": v(-3.12, 9.31) * mm, "end": v(-3.23, 9.31) * mm});
            skLineSegment(sketch, "E414", {"start": v(-3.23, 9.31) * mm, "end": v(-3.35, 9.31) * mm});
            skLineSegment(sketch, "E415", {"start": v(-3.35, 9.31) * mm, "end": v(-3.46, 9.31) * mm});
            skLineSegment(sketch, "E416", {"start": v(-3.46, 9.31) * mm, "end": v(-3.57, 9.31) * mm});
            skLineSegment(sketch, "E417", {"start": v(-3.57, 9.31) * mm, "end": v(-3.69, 9.31) * mm});
            skLineSegment(sketch, "E418", {"start": v(-3.69, 9.31) * mm, "end": v(-3.8, 9.31) * mm});
            skLineSegment(sketch, "E419", {"start": v(-3.8, 9.31) * mm, "end": v(-3.91, 9.31) * mm});
            skLineSegment(sketch, "E420", {"start": v(-3.91, 9.31) * mm, "end": v(-4.02, 9.31) * mm});
            skLineSegment(sketch, "E421", {"start": v(-4.02, 9.31) * mm, "end": v(-4.14, 9.31) * mm});
            skLineSegment(sketch, "E422", {"start": v(-4.14, 9.31) * mm, "end": v(-4.14, 9.44) * mm});
            skLineSegment(sketch, "E423", {"start": v(-4.14, 9.44) * mm, "end": v(-4.14, 9.57) * mm});
            skLineSegment(sketch, "E424", {"start": v(-4.14, 9.57) * mm, "end": v(-4.14, 9.7) * mm});
            skLineSegment(sketch, "E425", {"start": v(-4.14, 9.7) * mm, "end": v(-4.14, 9.83) * mm});
            skLineSegment(sketch, "E426", {"start": v(-4.14, 9.83) * mm, "end": v(-4.14, 9.96) * mm});
            skLineSegment(sketch, "E427", {"start": v(-4.14, 9.96) * mm, "end": v(-4.14, 10.09) * mm});
            skLineSegment(sketch, "E428", {"start": v(-4.14, 10.09) * mm, "end": v(-4.14, 10.22) * mm});
            skLineSegment(sketch, "E429", {"start": v(-4.14, 10.22) * mm, "end": v(-4.14, 10.34) * mm});
            skLineSegment(sketch, "E430", {"start": v(-4.14, 10.34) * mm, "end": v(-4.14, 10.47) * mm});
            skLineSegment(sketch, "E431", {"start": v(-4.14, 10.47) * mm, "end": v(-4.14, 10.6) * mm});
            skLineSegment(sketch, "E432", {"start": v(-4.14, 10.6) * mm, "end": v(-4.14, 10.73) * mm});
            skLineSegment(sketch, "E433", {"start": v(-4.14, 10.73) * mm, "end": v(-4.14, 10.86) * mm});
            skLineSegment(sketch, "E434", {"start": v(-4.14, 10.86) * mm, "end": v(-4.14, 11) * mm});
            skLineSegment(sketch, "E435", {"start": v(-4.14, 11) * mm, "end": v(-4.14, 11.12) * mm});
            skLineSegment(sketch, "E436", {"start": v(-4.14, 11.12) * mm, "end": v(-4.14, 11.25) * mm});
            skLineSegment(sketch, "E437", {"start": v(-4.14, 11.25) * mm, "end": v(-4.14, 11.38) * mm});
            skLineSegment(sketch, "E438", {"start": v(-4.14, 11.38) * mm, "end": v(-4.14, 11.6) * mm});
            skLineSegment(sketch, "E439", {"start": v(-4.14, 11.6) * mm, "end": v(-4.14, 11.83) * mm});
            skLineSegment(sketch, "E440", {"start": v(-4.14, 11.83) * mm, "end": v(-4.14, 12.06) * mm});
            skLineSegment(sketch, "E441", {"start": v(-4.14, 12.06) * mm, "end": v(-4.14, 12.28) * mm});
            skLineSegment(sketch, "E442", {"start": v(-4.14, 12.28) * mm, "end": v(-4.14, 12.51) * mm});
            skLineSegment(sketch, "E443", {"start": v(-4.14, 12.51) * mm, "end": v(-4.14, 12.74) * mm});
            skLineSegment(sketch, "E444", {"start": v(-4.14, 12.74) * mm, "end": v(-4.14, 12.96) * mm});
            skLineSegment(sketch, "E445", {"start": v(-4.14, 12.96) * mm, "end": v(-4.14, 13.19) * mm});
            skLineSegment(sketch, "E446", {"start": v(-4.14, 13.19) * mm, "end": v(-4.14, 13.42) * mm});
            skLineSegment(sketch, "E447", {"start": v(-4.14, 13.42) * mm, "end": v(-4.14, 13.64) * mm});
            skLineSegment(sketch, "E448", {"start": v(-4.14, 13.64) * mm, "end": v(-4.14, 13.87) * mm});
            skLineSegment(sketch, "E449", {"start": v(-4.14, 13.87) * mm, "end": v(-4.14, 14.1) * mm});
            skLineSegment(sketch, "E450", {"start": v(-4.14, 14.1) * mm, "end": v(-4.14, 14.32) * mm});
            skLineSegment(sketch, "E451", {"start": v(-4.14, 14.32) * mm, "end": v(-4.14, 14.55) * mm});
            skLineSegment(sketch, "E452", {"start": v(-4.14, 14.55) * mm, "end": v(-4.14, 14.77) * mm});
            skLineSegment(sketch, "E453", {"start": v(-4.14, 14.77) * mm, "end": v(-4.14, 15) * mm});
            skLineSegment(sketch, "E454", {"start": v(-4.14, 15) * mm, "end": v(-4.27, 14.95) * mm});
            skLineSegment(sketch, "E455", {"start": v(-4.27, 14.95) * mm, "end": v(-4.4, 14.9) * mm});
            skLineSegment(sketch, "E456", {"start": v(-4.4, 14.9) * mm, "end": v(-4.53, 14.84) * mm});
            skLineSegment(sketch, "E457", {"start": v(-4.53, 14.84) * mm, "end": v(-4.66, 14.8) * mm});
            skLineSegment(sketch, "E458", {"start": v(-4.66, 14.8) * mm, "end": v(-4.78, 14.74) * mm});
            skLineSegment(sketch, "E459", {"start": v(-4.78, 14.74) * mm, "end": v(-4.91, 14.69) * mm});
            skLineSegment(sketch, "E460", {"start": v(-4.91, 14.69) * mm, "end": v(-5.04, 14.64) * mm});
            skLineSegment(sketch, "E461", {"start": v(-5.04, 14.64) * mm, "end": v(-5.17, 14.59) * mm});
            skLineSegment(sketch, "E462", {"start": v(-5.17, 14.59) * mm, "end": v(-5.3, 14.53) * mm});
            skLineSegment(sketch, "E463", {"start": v(-5.3, 14.53) * mm, "end": v(-5.43, 14.48) * mm});
            skLineSegment(sketch, "E464", {"start": v(-5.43, 14.48) * mm, "end": v(-5.56, 14.43) * mm});
            skLineSegment(sketch, "E465", {"start": v(-5.56, 14.43) * mm, "end": v(-5.69, 14.38) * mm});
            skLineSegment(sketch, "E466", {"start": v(-5.69, 14.38) * mm, "end": v(-5.82, 14.33) * mm});
            skLineSegment(sketch, "E467", {"start": v(-5.82, 14.33) * mm, "end": v(-5.95, 14.28) * mm});
            skLineSegment(sketch, "E468", {"start": v(-5.95, 14.28) * mm, "end": v(-6.08, 14.22) * mm});
            skLineSegment(sketch, "E469", {"start": v(-6.08, 14.22) * mm, "end": v(-6.2, 14.17) * mm});
            skLineSegment(sketch, "E470", {"start": v(-6.2, 14.17) * mm, "end": v(-6.24, 14.16) * mm});
            skLineSegment(sketch, "E471", {"start": v(-6.24, 14.16) * mm, "end": v(-6.27, 14.15) * mm});
            skLineSegment(sketch, "E472", {"start": v(-6.27, 14.15) * mm, "end": v(-6.3, 14.13) * mm});
            skLineSegment(sketch, "E473", {"start": v(-6.3, 14.13) * mm, "end": v(-6.34, 14.12) * mm});
            skLineSegment(sketch, "E474", {"start": v(-6.34, 14.12) * mm, "end": v(-6.37, 14.1) * mm});
            skLineSegment(sketch, "E475", {"start": v(-6.37, 14.1) * mm, "end": v(-6.4, 14.1) * mm});
            skLineSegment(sketch, "E476", {"start": v(-6.4, 14.1) * mm, "end": v(-6.43, 14.08) * mm});
            skLineSegment(sketch, "E477", {"start": v(-6.43, 14.08) * mm, "end": v(-6.47, 14.07) * mm});
            skLineSegment(sketch, "E478", {"start": v(-6.47, 14.07) * mm, "end": v(-6.5, 14.06) * mm});
            skLineSegment(sketch, "E479", {"start": v(-6.5, 14.06) * mm, "end": v(-6.53, 14.04) * mm});
            skLineSegment(sketch, "E480", {"start": v(-6.53, 14.04) * mm, "end": v(-6.56, 14.03) * mm});
            skLineSegment(sketch, "E481", {"start": v(-6.56, 14.03) * mm, "end": v(-6.6, 14.02) * mm});
            skLineSegment(sketch, "E482", {"start": v(-6.6, 14.02) * mm, "end": v(-6.63, 14) * mm});
            skLineSegment(sketch, "E483", {"start": v(-6.63, 14) * mm, "end": v(-6.66, 14) * mm});
            skLineSegment(sketch, "E484", {"start": v(-6.66, 14) * mm, "end": v(-6.7, 13.98) * mm});
            skLineSegment(sketch, "E485", {"start": v(-6.7, 13.98) * mm, "end": v(-6.72, 13.97) * mm});
            skLineSegment(sketch, "E486", {"start": v(-6.72, 13.97) * mm, "end": v(-6.86, 13.65) * mm});
            skLineSegment(sketch, "E487", {"start": v(-6.86, 13.65) * mm, "end": v(-7, 13.33) * mm});
            skLineSegment(sketch, "E488", {"start": v(-7, 13.33) * mm, "end": v(-7.12, 13) * mm});
            skLineSegment(sketch, "E489", {"start": v(-7.12, 13) * mm, "end": v(-7.26, 12.69) * mm});
            skLineSegment(sketch, "E490", {"start": v(-7.26, 12.69) * mm, "end": v(-7.39, 12.37) * mm});
            skLineSegment(sketch, "E491", {"start": v(-7.39, 12.37) * mm, "end": v(-7.52, 12.05) * mm});
            skLineSegment(sketch, "E492", {"start": v(-7.52, 12.05) * mm, "end": v(-7.66, 11.73) * mm});
            skLineSegment(sketch, "E493", {"start": v(-7.66, 11.73) * mm, "end": v(-7.79, 11.4) * mm});
            skLineSegment(sketch, "E494", {"start": v(-7.79, 11.4) * mm, "end": v(-7.92, 11.1) * mm});
            skLineSegment(sketch, "E495", {"start": v(-7.92, 11.1) * mm, "end": v(-8.06, 10.77) * mm});
            skLineSegment(sketch, "E496", {"start": v(-8.06, 10.77) * mm, "end": v(-8.19, 10.45) * mm});
            skLineSegment(sketch, "E497", {"start": v(-8.19, 10.45) * mm, "end": v(-8.32, 10.13) * mm});
            skLineSegment(sketch, "E498", {"start": v(-8.32, 10.13) * mm, "end": v(-8.45, 9.81) * mm});
            skLineSegment(sketch, "E499", {"start": v(-8.45, 9.81) * mm, "end": v(-8.59, 9.5) * mm});
            skLineSegment(sketch, "E500", {"start": v(-8.59, 9.5) * mm, "end": v(-8.72, 9.17) * mm});
            skLineSegment(sketch, "E501", {"start": v(-8.72, 9.17) * mm, "end": v(-8.85, 8.85) * mm});
            skLineSegment(sketch, "E502", {"start": v(-8.85, 8.85) * mm, "end": v(-9.17, 8.72) * mm});
            skLineSegment(sketch, "E503", {"start": v(-9.17, 8.72) * mm, "end": v(-9.5, 8.59) * mm});
            skLineSegment(sketch, "E504", {"start": v(-9.5, 8.59) * mm, "end": v(-9.81, 8.45) * mm});
            skLineSegment(sketch, "E505", {"start": v(-9.81, 8.45) * mm, "end": v(-10.13, 8.32) * mm});
            skLineSegment(sketch, "E506", {"start": v(-10.13, 8.32) * mm, "end": v(-10.45, 8.19) * mm});
            skLineSegment(sketch, "E507", {"start": v(-10.45, 8.19) * mm, "end": v(-10.77, 8.06) * mm});
            skLineSegment(sketch, "E508", {"start": v(-10.77, 8.06) * mm, "end": v(-11.1, 7.92) * mm});
            skLineSegment(sketch, "E509", {"start": v(-11.1, 7.92) * mm, "end": v(-11.4, 7.79) * mm});
            skLineSegment(sketch, "E510", {"start": v(-11.4, 7.79) * mm, "end": v(-11.73, 7.66) * mm});
            skLineSegment(sketch, "E511", {"start": v(-11.73, 7.66) * mm, "end": v(-12.05, 7.52) * mm});
            skLineSegment(sketch, "E512", {"start": v(-12.05, 7.52) * mm, "end": v(-12.37, 7.39) * mm});
            skLineSegment(sketch, "E513", {"start": v(-12.37, 7.39) * mm, "end": v(-12.69, 7.26) * mm});
            skLineSegment(sketch, "E514", {"start": v(-12.69, 7.26) * mm, "end": v(-13, 7.12) * mm});
            skLineSegment(sketch, "E515", {"start": v(-13, 7.12) * mm, "end": v(-13.33, 7) * mm});
            skLineSegment(sketch, "E516", {"start": v(-13.33, 7) * mm, "end": v(-13.65, 6.86) * mm});
            skLineSegment(sketch, "E517", {"start": v(-13.65, 6.86) * mm, "end": v(-13.97, 6.72) * mm});
            skLineSegment(sketch, "E518", {"start": v(-13.97, 6.72) * mm, "end": v(-13.98, 6.7) * mm});
            skLineSegment(sketch, "E519", {"start": v(-13.98, 6.7) * mm, "end": v(-14, 6.66) * mm});
            skLineSegment(sketch, "E520", {"start": v(-14, 6.66) * mm, "end": v(-14, 6.63) * mm});
            skLineSegment(sketch, "E521", {"start": v(-14, 6.63) * mm, "end": v(-14.02, 6.6) * mm});
            skLineSegment(sketch, "E522", {"start": v(-14.02, 6.6) * mm, "end": v(-14.03, 6.56) * mm});
            skLineSegment(sketch, "E523", {"start": v(-14.03, 6.56) * mm, "end": v(-14.04, 6.53) * mm});
            skLineSegment(sketch, "E524", {"start": v(-14.04, 6.53) * mm, "end": v(-14.06, 6.5) * mm});
            skLineSegment(sketch, "E525", {"start": v(-14.06, 6.5) * mm, "end": v(-14.07, 6.47) * mm});
            skLineSegment(sketch, "E526", {"start": v(-14.07, 6.47) * mm, "end": v(-14.08, 6.43) * mm});
            skLineSegment(sketch, "E527", {"start": v(-14.08, 6.43) * mm, "end": v(-14.1, 6.4) * mm});
            skLineSegment(sketch, "E528", {"start": v(-14.1, 6.4) * mm, "end": v(-14.1, 6.37) * mm});
            skLineSegment(sketch, "E529", {"start": v(-14.1, 6.37) * mm, "end": v(-14.12, 6.34) * mm});
            skLineSegment(sketch, "E530", {"start": v(-14.12, 6.34) * mm, "end": v(-14.13, 6.3) * mm});
            skLineSegment(sketch, "E531", {"start": v(-14.13, 6.3) * mm, "end": v(-14.15, 6.27) * mm});
            skLineSegment(sketch, "E532", {"start": v(-14.15, 6.27) * mm, "end": v(-14.16, 6.24) * mm});
            skLineSegment(sketch, "E533", {"start": v(-14.16, 6.24) * mm, "end": v(-14.17, 6.2) * mm});
            skLineSegment(sketch, "E534", {"start": v(-14.17, 6.2) * mm, "end": v(-14.22, 6.08) * mm});
            skLineSegment(sketch, "E535", {"start": v(-14.22, 6.08) * mm, "end": v(-14.28, 5.95) * mm});
            skLineSegment(sketch, "E536", {"start": v(-14.28, 5.95) * mm, "end": v(-14.33, 5.82) * mm});
            skLineSegment(sketch, "E537", {"start": v(-14.33, 5.82) * mm, "end": v(-14.38, 5.69) * mm});
            skLineSegment(sketch, "E538", {"start": v(-14.38, 5.69) * mm, "end": v(-14.43, 5.56) * mm});
            skLineSegment(sketch, "E539", {"start": v(-14.43, 5.56) * mm, "end": v(-14.48, 5.43) * mm});
            skLineSegment(sketch, "E540", {"start": v(-14.48, 5.43) * mm, "end": v(-14.53, 5.3) * mm});
            skLineSegment(sketch, "E541", {"start": v(-14.53, 5.3) * mm, "end": v(-14.59, 5.17) * mm});
            skLineSegment(sketch, "E542", {"start": v(-14.59, 5.17) * mm, "end": v(-14.64, 5.04) * mm});
            skLineSegment(sketch, "E543", {"start": v(-14.64, 5.04) * mm, "end": v(-14.69, 4.91) * mm});
            skLineSegment(sketch, "E544", {"start": v(-14.69, 4.91) * mm, "end": v(-14.74, 4.78) * mm});
            skLineSegment(sketch, "E545", {"start": v(-14.74, 4.78) * mm, "end": v(-14.8, 4.66) * mm});
            skLineSegment(sketch, "E546", {"start": v(-14.8, 4.66) * mm, "end": v(-14.84, 4.53) * mm});
            skLineSegment(sketch, "E547", {"start": v(-14.84, 4.53) * mm, "end": v(-14.9, 4.4) * mm});
            skLineSegment(sketch, "E548", {"start": v(-14.9, 4.4) * mm, "end": v(-14.95, 4.27) * mm});
            skLineSegment(sketch, "E549", {"start": v(-14.95, 4.27) * mm, "end": v(-15, 4.14) * mm});
            skLineSegment(sketch, "E550", {"start": v(-15, 4.14) * mm, "end": v(-14.77, 4.14) * mm});
            skLineSegment(sketch, "E551", {"start": v(-14.77, 4.14) * mm, "end": v(-14.55, 4.14) * mm});
            skLineSegment(sketch, "E552", {"start": v(-14.55, 4.14) * mm, "end": v(-14.32, 4.14) * mm});
            skLineSegment(sketch, "E553", {"start": v(-14.32, 4.14) * mm, "end": v(-14.1, 4.14) * mm});
            skLineSegment(sketch, "E554", {"start": v(-14.1, 4.14) * mm, "end": v(-13.87, 4.14) * mm});
            skLineSegment(sketch, "E555", {"start": v(-13.87, 4.14) * mm, "end": v(-13.64, 4.14) * mm});
            skLineSegment(sketch, "E556", {"start": v(-13.64, 4.14) * mm, "end": v(-13.42, 4.14) * mm});
            skLineSegment(sketch, "E557", {"start": v(-13.42, 4.14) * mm, "end": v(-13.19, 4.14) * mm});
            skLineSegment(sketch, "E558", {"start": v(-13.19, 4.14) * mm, "end": v(-12.96, 4.14) * mm});
            skLineSegment(sketch, "E559", {"start": v(-12.96, 4.14) * mm, "end": v(-12.74, 4.14) * mm});
            skLineSegment(sketch, "E560", {"start": v(-12.74, 4.14) * mm, "end": v(-12.51, 4.14) * mm});
            skLineSegment(sketch, "E561", {"start": v(-12.51, 4.14) * mm, "end": v(-12.28, 4.14) * mm});
            skLineSegment(sketch, "E562", {"start": v(-12.28, 4.14) * mm, "end": v(-12.06, 4.14) * mm});
            skLineSegment(sketch, "E563", {"start": v(-12.06, 4.14) * mm, "end": v(-11.83, 4.14) * mm});
            skLineSegment(sketch, "E564", {"start": v(-11.83, 4.14) * mm, "end": v(-11.6, 4.14) * mm});
            skLineSegment(sketch, "E565", {"start": v(-11.6, 4.14) * mm, "end": v(-11.38, 4.14) * mm});
            skLineSegment(sketch, "E566", {"start": v(-11.38, 4.14) * mm, "end": v(-11.25, 4.14) * mm});
            skLineSegment(sketch, "E567", {"start": v(-11.25, 4.14) * mm, "end": v(-11.12, 4.14) * mm});
            skLineSegment(sketch, "E568", {"start": v(-11.12, 4.14) * mm, "end": v(-11, 4.14) * mm});
            skLineSegment(sketch, "E569", {"start": v(-11, 4.14) * mm, "end": v(-10.86, 4.14) * mm});
            skLineSegment(sketch, "E570", {"start": v(-10.86, 4.14) * mm, "end": v(-10.73, 4.14) * mm});
            skLineSegment(sketch, "E571", {"start": v(-10.73, 4.14) * mm, "end": v(-10.6, 4.14) * mm});
            skLineSegment(sketch, "E572", {"start": v(-10.6, 4.14) * mm, "end": v(-10.47, 4.14) * mm});
            skLineSegment(sketch, "E573", {"start": v(-10.47, 4.14) * mm, "end": v(-10.34, 4.14) * mm});
            skLineSegment(sketch, "E574", {"start": v(-10.34, 4.14) * mm, "end": v(-10.22, 4.14) * mm});
            skLineSegment(sketch, "E575", {"start": v(-10.22, 4.14) * mm, "end": v(-10.09, 4.14) * mm});
            skLineSegment(sketch, "E576", {"start": v(-10.09, 4.14) * mm, "end": v(-9.96, 4.14) * mm});
            skLineSegment(sketch, "E577", {"start": v(-9.96, 4.14) * mm, "end": v(-9.83, 4.14) * mm});
            skLineSegment(sketch, "E578", {"start": v(-9.83, 4.14) * mm, "end": v(-9.7, 4.14) * mm});
            skLineSegment(sketch, "E579", {"start": v(-9.7, 4.14) * mm, "end": v(-9.57, 4.14) * mm});
            skLineSegment(sketch, "E580", {"start": v(-9.57, 4.14) * mm, "end": v(-9.44, 4.14) * mm});
            skLineSegment(sketch, "E581", {"start": v(-9.44, 4.14) * mm, "end": v(-9.31, 4.14) * mm});
            skLineSegment(sketch, "E582", {"start": v(-9.31, 4.14) * mm, "end": v(-9.31, 4.02) * mm});
            skLineSegment(sketch, "E583", {"start": v(-9.31, 4.02) * mm, "end": v(-9.31, 3.91) * mm});
            skLineSegment(sketch, "E584", {"start": v(-9.31, 3.91) * mm, "end": v(-9.31, 3.8) * mm});
            skLineSegment(sketch, "E585", {"start": v(-9.31, 3.8) * mm, "end": v(-9.31, 3.69) * mm});
            skLineSegment(sketch, "E586", {"start": v(-9.31, 3.69) * mm, "end": v(-9.31, 3.57) * mm});
            skLineSegment(sketch, "E587", {"start": v(-9.31, 3.57) * mm, "end": v(-9.31, 3.46) * mm});
            skLineSegment(sketch, "E588", {"start": v(-9.31, 3.46) * mm, "end": v(-9.31, 3.35) * mm});
            skLineSegment(sketch, "E589", {"start": v(-9.31, 3.35) * mm, "end": v(-9.31, 3.23) * mm});
            skLineSegment(sketch, "E590", {"start": v(-9.31, 3.23) * mm, "end": v(-9.31, 3.12) * mm});
            skLineSegment(sketch, "E591", {"start": v(-9.31, 3.12) * mm, "end": v(-9.31, 3) * mm});
            skLineSegment(sketch, "E592", {"start": v(-9.31, 3) * mm, "end": v(-9.31, 2.9) * mm});
            skLineSegment(sketch, "E593", {"start": v(-9.31, 2.9) * mm, "end": v(-9.31, 2.78) * mm});
            skLineSegment(sketch, "E594", {"start": v(-9.31, 2.78) * mm, "end": v(-9.31, 2.67) * mm});
            skLineSegment(sketch, "E595", {"start": v(-9.31, 2.67) * mm, "end": v(-9.31, 2.55) * mm});
            skLineSegment(sketch, "E596", {"start": v(-9.31, 2.55) * mm, "end": v(-9.31, 2.44) * mm});
            skLineSegment(sketch, "E597", {"start": v(-9.31, 2.44) * mm, "end": v(-9.31, 2.33) * mm});
            skLineSegment(sketch, "E598", {"start": v(-9.31, 2.33) * mm, "end": v(-9.3, 2.2) * mm});
            skLineSegment(sketch, "E599", {"start": v(-9.3, 2.2) * mm, "end": v(-9.28, 2.07) * mm});
            skLineSegment(sketch, "E600", {"start": v(-9.28, 2.07) * mm, "end": v(-9.25, 1.94) * mm});
            skLineSegment(sketch, "E601", {"start": v(-9.25, 1.94) * mm, "end": v(-9.2, 1.82) * mm});
            skLineSegment(sketch, "E602", {"start": v(-9.2, 1.82) * mm, "end": v(-9.15, 1.71) * mm});
            skLineSegment(sketch, "E603", {"start": v(-9.15, 1.71) * mm, "end": v(-9.09, 1.6) * mm});
            skLineSegment(sketch, "E604", {"start": v(-9.09, 1.6) * mm, "end": v(-9.02, 1.5) * mm});
            skLineSegment(sketch, "E605", {"start": v(-9.02, 1.5) * mm, "end": v(-8.93, 1.41) * mm});
            skLineSegment(sketch, "E606", {"start": v(-8.93, 1.41) * mm, "end": v(-8.84, 1.33) * mm});
            skLineSegment(sketch, "E607", {"start": v(-8.84, 1.33) * mm, "end": v(-8.74, 1.26) * mm});
            skLineSegment(sketch, "E608", {"start": v(-8.74, 1.26) * mm, "end": v(-8.63, 1.2) * mm});
            skLineSegment(sketch, "E609", {"start": v(-8.63, 1.2) * mm, "end": v(-8.52, 1.14) * mm});
            skLineSegment(sketch, "E610", {"start": v(-8.52, 1.14) * mm, "end": v(-8.4, 1.1) * mm});
            skLineSegment(sketch, "E611", {"start": v(-8.4, 1.1) * mm, "end": v(-8.28, 1.06) * mm});
            skLineSegment(sketch, "E612", {"start": v(-8.28, 1.06) * mm, "end": v(-8.15, 1.04) * mm});
            skLineSegment(sketch, "E613", {"start": v(-8.15, 1.04) * mm, "end": v(-8.02, 1.03) * mm});
            skLineSegment(sketch, "E614", {"start": v(-8.02, 1.03) * mm, "end": v(-7.9, 1.03) * mm});
            skLineSegment(sketch, "E615", {"start": v(-7.9, 1.03) * mm, "end": v(-7.8, 1.03) * mm});
            skLineSegment(sketch, "E616", {"start": v(-7.8, 1.03) * mm, "end": v(-7.68, 1.03) * mm});
            skLineSegment(sketch, "E617", {"start": v(-7.68, 1.03) * mm, "end": v(-7.56, 1.03) * mm});
            skLineSegment(sketch, "E618", {"start": v(-7.56, 1.03) * mm, "end": v(-7.45, 1.03) * mm});
            skLineSegment(sketch, "E619", {"start": v(-7.45, 1.03) * mm, "end": v(-7.34, 1.03) * mm});
            skLineSegment(sketch, "E620", {"start": v(-7.34, 1.03) * mm, "end": v(-7.23, 1.03) * mm});
            skLineSegment(sketch, "E621", {"start": v(-7.23, 1.03) * mm, "end": v(-7.11, 1.03) * mm});
            skLineSegment(sketch, "E622", {"start": v(-7.11, 1.03) * mm, "end": v(-7, 1.03) * mm});
            skLineSegment(sketch, "E623", {"start": v(-7, 1.03) * mm, "end": v(-6.89, 1.03) * mm});
            skLineSegment(sketch, "E624", {"start": v(-6.89, 1.03) * mm, "end": v(-6.77, 1.03) * mm});
            skLineSegment(sketch, "E625", {"start": v(-6.77, 1.03) * mm, "end": v(-6.66, 1.03) * mm});
            skLineSegment(sketch, "E626", {"start": v(-6.66, 1.03) * mm, "end": v(-6.55, 1.03) * mm});
            skLineSegment(sketch, "E627", {"start": v(-6.55, 1.03) * mm, "end": v(-6.43, 1.03) * mm});
            skLineSegment(sketch, "E628", {"start": v(-6.43, 1.03) * mm, "end": v(-6.32, 1.03) * mm});
            skLineSegment(sketch, "E629", {"start": v(-6.32, 1.03) * mm, "end": v(-6.2, 1.03) * mm});
            skLineSegment(sketch, "E630", {"start": v(-6.2, 1.03) * mm, "end": v(-6.2, 0.97) * mm});
            skLineSegment(sketch, "E631", {"start": v(-6.2, 0.97) * mm, "end": v(-6.2, 0.9) * mm});
            skLineSegment(sketch, "E632", {"start": v(-6.2, 0.9) * mm, "end": v(-6.2, 0.84) * mm});
            skLineSegment(sketch, "E633", {"start": v(-6.2, 0.84) * mm, "end": v(-6.2, 0.78) * mm});
            skLineSegment(sketch, "E634", {"start": v(-6.2, 0.78) * mm, "end": v(-6.2, 0.71) * mm});
            skLineSegment(sketch, "E635", {"start": v(-6.2, 0.71) * mm, "end": v(-6.2, 0.65) * mm});
            skLineSegment(sketch, "E636", {"start": v(-6.2, 0.65) * mm, "end": v(-6.2, 0.58) * mm});
            skLineSegment(sketch, "E637", {"start": v(-6.2, 0.58) * mm, "end": v(-6.2, 0.52) * mm});
            skLineSegment(sketch, "E638", {"start": v(-6.2, 0.52) * mm, "end": v(-6.2, 0.45) * mm});
            skLineSegment(sketch, "E639", {"start": v(-6.2, 0.45) * mm, "end": v(-6.2, 0.39) * mm});
            skLineSegment(sketch, "E640", {"start": v(-6.2, 0.39) * mm, "end": v(-6.2, 0.32) * mm});
            skLineSegment(sketch, "E641", {"start": v(-6.2, 0.32) * mm, "end": v(-6.2, 0.26) * mm});
            skLineSegment(sketch, "E642", {"start": v(-6.2, 0.26) * mm, "end": v(-6.2, 0.2) * mm});
            skLineSegment(sketch, "E643", {"start": v(-6.2, 0.2) * mm, "end": v(-6.2, 0.13) * mm});
            skLineSegment(sketch, "E644", {"start": v(-6.2, 0.13) * mm, "end": v(-6.2, 0.06) * mm});
            skLineSegment(sketch, "E645", {"start": v(-6.2, 0.06) * mm, "end": v(-6.2, 0) * mm});
            skLineSegment(sketch, "E646", {"start": v(-6.2, 0) * mm, "end": v(-6.2, -0.06) * mm});
            skLineSegment(sketch, "E647", {"start": v(-6.2, -0.06) * mm, "end": v(-6.2, -0.13) * mm});
            skLineSegment(sketch, "E648", {"start": v(-6.2, -0.13) * mm, "end": v(-6.2, -0.2) * mm});
            skLineSegment(sketch, "E649", {"start": v(-6.2, -0.2) * mm, "end": v(-6.2, -0.26) * mm});
            skLineSegment(sketch, "E650", {"start": v(-6.2, -0.26) * mm, "end": v(-6.2, -0.32) * mm});
            skLineSegment(sketch, "E651", {"start": v(-6.2, -0.32) * mm, "end": v(-6.2, -0.39) * mm});
            skLineSegment(sketch, "E652", {"start": v(-6.2, -0.39) * mm, "end": v(-6.2, -0.45) * mm});
            skLineSegment(sketch, "E653", {"start": v(-6.2, -0.45) * mm, "end": v(-6.2, -0.52) * mm});
            skLineSegment(sketch, "E654", {"start": v(-6.2, -0.52) * mm, "end": v(-6.2, -0.58) * mm});
            skLineSegment(sketch, "E655", {"start": v(-6.2, -0.58) * mm, "end": v(-6.2, -0.65) * mm});
            skLineSegment(sketch, "E656", {"start": v(-6.2, -0.65) * mm, "end": v(-6.2, -0.71) * mm});
            skLineSegment(sketch, "E657", {"start": v(-6.2, -0.71) * mm, "end": v(-6.2, -0.78) * mm});
            skLineSegment(sketch, "E658", {"start": v(-6.2, -0.78) * mm, "end": v(-6.2, -0.84) * mm});
            skLineSegment(sketch, "E659", {"start": v(-6.2, -0.84) * mm, "end": v(-6.2, -0.9) * mm});
            skLineSegment(sketch, "E660", {"start": v(-6.2, -0.9) * mm, "end": v(-6.2, -0.97) * mm});
            skLineSegment(sketch, "E661", {"start": v(-6.2, -0.97) * mm, "end": v(-6.2, -1.03) * mm});
            skLineSegment(sketch, "E662", {"start": v(-6.2, -1.03) * mm, "end": v(-6.32, -1.03) * mm});
            skLineSegment(sketch, "E663", {"start": v(-6.32, -1.03) * mm, "end": v(-6.43, -1.03) * mm});
            skLineSegment(sketch, "E664", {"start": v(-6.43, -1.03) * mm, "end": v(-6.55, -1.03) * mm});
            skLineSegment(sketch, "E665", {"start": v(-6.55, -1.03) * mm, "end": v(-6.66, -1.03) * mm});
            skLineSegment(sketch, "E666", {"start": v(-6.66, -1.03) * mm, "end": v(-6.77, -1.03) * mm});
            skLineSegment(sketch, "E667", {"start": v(-6.77, -1.03) * mm, "end": v(-6.89, -1.03) * mm});
            skLineSegment(sketch, "E668", {"start": v(-6.89, -1.03) * mm, "end": v(-7, -1.03) * mm});
            skLineSegment(sketch, "E669", {"start": v(-7, -1.03) * mm, "end": v(-7.11, -1.03) * mm});
            skLineSegment(sketch, "E670", {"start": v(-7.11, -1.03) * mm, "end": v(-7.23, -1.03) * mm});
            skLineSegment(sketch, "E671", {"start": v(-7.23, -1.03) * mm, "end": v(-7.34, -1.03) * mm});
            skLineSegment(sketch, "E672", {"start": v(-7.34, -1.03) * mm, "end": v(-7.45, -1.03) * mm});
            skLineSegment(sketch, "E673", {"start": v(-7.45, -1.03) * mm, "end": v(-7.56, -1.03) * mm});
            skLineSegment(sketch, "E674", {"start": v(-7.56, -1.03) * mm, "end": v(-7.68, -1.03) * mm});
            skLineSegment(sketch, "E675", {"start": v(-7.68, -1.03) * mm, "end": v(-7.8, -1.03) * mm});
            skLineSegment(sketch, "E676", {"start": v(-7.8, -1.03) * mm, "end": v(-7.9, -1.03) * mm});
            skLineSegment(sketch, "E677", {"start": v(-7.9, -1.03) * mm, "end": v(-8.02, -1.03) * mm});
            skLineSegment(sketch, "E678", {"start": v(-8.02, -1.03) * mm, "end": v(-8.15, -1.04) * mm});
            skLineSegment(sketch, "E679", {"start": v(-8.15, -1.04) * mm, "end": v(-8.28, -1.06) * mm});
            skLineSegment(sketch, "E680", {"start": v(-8.28, -1.06) * mm, "end": v(-8.4, -1.1) * mm});
            skLineSegment(sketch, "E681", {"start": v(-8.4, -1.1) * mm, "end": v(-8.52, -1.14) * mm});
            skLineSegment(sketch, "E682", {"start": v(-8.52, -1.14) * mm, "end": v(-8.63, -1.2) * mm});
            skLineSegment(sketch, "E683", {"start": v(-8.63, -1.2) * mm, "end": v(-8.74, -1.26) * mm});
            skLineSegment(sketch, "E684", {"start": v(-8.74, -1.26) * mm, "end": v(-8.84, -1.33) * mm});
            skLineSegment(sketch, "E685", {"start": v(-8.84, -1.33) * mm, "end": v(-8.93, -1.41) * mm});
            skLineSegment(sketch, "E686", {"start": v(-8.93, -1.41) * mm, "end": v(-9.02, -1.5) * mm});
            skLineSegment(sketch, "E687", {"start": v(-9.02, -1.5) * mm, "end": v(-9.09, -1.6) * mm});
            skLineSegment(sketch, "E688", {"start": v(-9.09, -1.6) * mm, "end": v(-9.15, -1.71) * mm});
            skLineSegment(sketch, "E689", {"start": v(-9.15, -1.71) * mm, "end": v(-9.2, -1.82) * mm});
            skLineSegment(sketch, "E690", {"start": v(-9.2, -1.82) * mm, "end": v(-9.25, -1.94) * mm});
            skLineSegment(sketch, "E691", {"start": v(-9.25, -1.94) * mm, "end": v(-9.28, -2.07) * mm});
            skLineSegment(sketch, "E692", {"start": v(-9.28, -2.07) * mm, "end": v(-9.3, -2.2) * mm});
            skLineSegment(sketch, "E693", {"start": v(-9.3, -2.2) * mm, "end": v(-9.31, -2.33) * mm});
            skLineSegment(sketch, "E694", {"start": v(-9.31, -2.33) * mm, "end": v(-9.31, -2.44) * mm});
            skLineSegment(sketch, "E695", {"start": v(-9.31, -2.44) * mm, "end": v(-9.31, -2.55) * mm});
            skLineSegment(sketch, "E696", {"start": v(-9.31, -2.55) * mm, "end": v(-9.31, -2.67) * mm});
            skLineSegment(sketch, "E697", {"start": v(-9.31, -2.67) * mm, "end": v(-9.31, -2.78) * mm});
            skLineSegment(sketch, "E698", {"start": v(-9.31, -2.78) * mm, "end": v(-9.31, -2.9) * mm});
            skLineSegment(sketch, "E699", {"start": v(-9.31, -2.9) * mm, "end": v(-9.31, -3) * mm});
            skLineSegment(sketch, "E700", {"start": v(-9.31, -3) * mm, "end": v(-9.31, -3.12) * mm});
            skLineSegment(sketch, "E701", {"start": v(-9.31, -3.12) * mm, "end": v(-9.31, -3.23) * mm});
            skLineSegment(sketch, "E702", {"start": v(-9.31, -3.23) * mm, "end": v(-9.31, -3.35) * mm});
            skLineSegment(sketch, "E703", {"start": v(-9.31, -3.35) * mm, "end": v(-9.31, -3.46) * mm});
            skLineSegment(sketch, "E704", {"start": v(-9.31, -3.46) * mm, "end": v(-9.31, -3.57) * mm});
            skLineSegment(sketch, "E705", {"start": v(-9.31, -3.57) * mm, "end": v(-9.31, -3.69) * mm});
            skLineSegment(sketch, "E706", {"start": v(-9.31, -3.69) * mm, "end": v(-9.31, -3.8) * mm});
            skLineSegment(sketch, "E707", {"start": v(-9.31, -3.8) * mm, "end": v(-9.31, -3.91) * mm});
            skLineSegment(sketch, "E708", {"start": v(-9.31, -3.91) * mm, "end": v(-9.31, -4.02) * mm});
            skLineSegment(sketch, "E709", {"start": v(-9.31, -4.02) * mm, "end": v(-9.31, -4.14) * mm});
            skLineSegment(sketch, "E710", {"start": v(-9.31, -4.14) * mm, "end": v(-9.44, -4.14) * mm});
            skLineSegment(sketch, "E711", {"start": v(-9.44, -4.14) * mm, "end": v(-9.57, -4.14) * mm});
            skLineSegment(sketch, "E712", {"start": v(-9.57, -4.14) * mm, "end": v(-9.7, -4.14) * mm});
            skLineSegment(sketch, "E713", {"start": v(-9.7, -4.14) * mm, "end": v(-9.83, -4.14) * mm});
            skLineSegment(sketch, "E714", {"start": v(-9.83, -4.14) * mm, "end": v(-9.96, -4.14) * mm});
            skLineSegment(sketch, "E715", {"start": v(-9.96, -4.14) * mm, "end": v(-10.09, -4.14) * mm});
            skLineSegment(sketch, "E716", {"start": v(-10.09, -4.14) * mm, "end": v(-10.22, -4.14) * mm});
            skLineSegment(sketch, "E717", {"start": v(-10.22, -4.14) * mm, "end": v(-10.34, -4.14) * mm});
            skLineSegment(sketch, "E718", {"start": v(-10.34, -4.14) * mm, "end": v(-10.47, -4.14) * mm});
            skLineSegment(sketch, "E719", {"start": v(-10.47, -4.14) * mm, "end": v(-10.6, -4.14) * mm});
            skLineSegment(sketch, "E720", {"start": v(-10.6, -4.14) * mm, "end": v(-10.73, -4.14) * mm});
            skLineSegment(sketch, "E721", {"start": v(-10.73, -4.14) * mm, "end": v(-10.86, -4.14) * mm});
            skLineSegment(sketch, "E722", {"start": v(-10.86, -4.14) * mm, "end": v(-11, -4.14) * mm});
            skLineSegment(sketch, "E723", {"start": v(-11, -4.14) * mm, "end": v(-11.12, -4.14) * mm});
            skLineSegment(sketch, "E724", {"start": v(-11.12, -4.14) * mm, "end": v(-11.25, -4.14) * mm});
            skLineSegment(sketch, "E725", {"start": v(-11.25, -4.14) * mm, "end": v(-11.38, -4.14) * mm});
            skLineSegment(sketch, "E726", {"start": v(-11.38, -4.14) * mm, "end": v(-11.6, -4.14) * mm});
            skLineSegment(sketch, "E727", {"start": v(-11.6, -4.14) * mm, "end": v(-11.83, -4.14) * mm});
            skLineSegment(sketch, "E728", {"start": v(-11.83, -4.14) * mm, "end": v(-12.06, -4.14) * mm});
            skLineSegment(sketch, "E729", {"start": v(-12.06, -4.14) * mm, "end": v(-12.28, -4.14) * mm});
            skLineSegment(sketch, "E730", {"start": v(-12.28, -4.14) * mm, "end": v(-12.51, -4.14) * mm});
            skLineSegment(sketch, "E731", {"start": v(-12.51, -4.14) * mm, "end": v(-12.74, -4.14) * mm});
            skLineSegment(sketch, "E732", {"start": v(-12.74, -4.14) * mm, "end": v(-12.96, -4.14) * mm});
            skLineSegment(sketch, "E733", {"start": v(-12.96, -4.14) * mm, "end": v(-13.19, -4.14) * mm});
            skLineSegment(sketch, "E734", {"start": v(-13.19, -4.14) * mm, "end": v(-13.42, -4.14) * mm});
            skLineSegment(sketch, "E735", {"start": v(-13.42, -4.14) * mm, "end": v(-13.64, -4.14) * mm});
            skLineSegment(sketch, "E736", {"start": v(-13.64, -4.14) * mm, "end": v(-13.87, -4.14) * mm});
            skLineSegment(sketch, "E737", {"start": v(-13.87, -4.14) * mm, "end": v(-14.1, -4.14) * mm});
            skLineSegment(sketch, "E738", {"start": v(-14.1, -4.14) * mm, "end": v(-14.32, -4.14) * mm});
            skLineSegment(sketch, "E739", {"start": v(-14.32, -4.14) * mm, "end": v(-14.55, -4.14) * mm});
            skLineSegment(sketch, "E740", {"start": v(-14.55, -4.14) * mm, "end": v(-14.77, -4.14) * mm});
            skLineSegment(sketch, "E741", {"start": v(-14.77, -4.14) * mm, "end": v(-15, -4.14) * mm});
            skLineSegment(sketch, "E742", {"start": v(-15, -4.14) * mm, "end": v(-14.95, -4.27) * mm});
            skLineSegment(sketch, "E743", {"start": v(-14.95, -4.27) * mm, "end": v(-14.9, -4.4) * mm});
            skLineSegment(sketch, "E744", {"start": v(-14.9, -4.4) * mm, "end": v(-14.84, -4.53) * mm});
            skLineSegment(sketch, "E745", {"start": v(-14.84, -4.53) * mm, "end": v(-14.8, -4.66) * mm});
            skLineSegment(sketch, "E746", {"start": v(-14.8, -4.66) * mm, "end": v(-14.74, -4.78) * mm});
            skLineSegment(sketch, "E747", {"start": v(-14.74, -4.78) * mm, "end": v(-14.69, -4.91) * mm});
            skLineSegment(sketch, "E748", {"start": v(-14.69, -4.91) * mm, "end": v(-14.64, -5.04) * mm});
            skLineSegment(sketch, "E749", {"start": v(-14.64, -5.04) * mm, "end": v(-14.59, -5.17) * mm});
            skLineSegment(sketch, "E750", {"start": v(-14.59, -5.17) * mm, "end": v(-14.53, -5.3) * mm});
            skLineSegment(sketch, "E751", {"start": v(-14.53, -5.3) * mm, "end": v(-14.48, -5.43) * mm});
            skLineSegment(sketch, "E752", {"start": v(-14.48, -5.43) * mm, "end": v(-14.43, -5.56) * mm});
            skLineSegment(sketch, "E753", {"start": v(-14.43, -5.56) * mm, "end": v(-14.38, -5.69) * mm});
            skLineSegment(sketch, "E754", {"start": v(-14.38, -5.69) * mm, "end": v(-14.33, -5.82) * mm});
            skLineSegment(sketch, "E755", {"start": v(-14.33, -5.82) * mm, "end": v(-14.28, -5.95) * mm});
            skLineSegment(sketch, "E756", {"start": v(-14.28, -5.95) * mm, "end": v(-14.22, -6.08) * mm});
            skLineSegment(sketch, "E757", {"start": v(-14.22, -6.08) * mm, "end": v(-14.17, -6.2) * mm});
            skLineSegment(sketch, "E758", {"start": v(-14.17, -6.2) * mm, "end": v(-14.16, -6.24) * mm});
            skLineSegment(sketch, "E759", {"start": v(-14.16, -6.24) * mm, "end": v(-14.15, -6.27) * mm});
            skLineSegment(sketch, "E760", {"start": v(-14.15, -6.27) * mm, "end": v(-14.13, -6.3) * mm});
            skLineSegment(sketch, "E761", {"start": v(-14.13, -6.3) * mm, "end": v(-14.12, -6.34) * mm});
            skLineSegment(sketch, "E762", {"start": v(-14.12, -6.34) * mm, "end": v(-14.1, -6.37) * mm});
            skLineSegment(sketch, "E763", {"start": v(-14.1, -6.37) * mm, "end": v(-14.1, -6.4) * mm});
            skLineSegment(sketch, "E764", {"start": v(-14.1, -6.4) * mm, "end": v(-14.08, -6.43) * mm});
            skLineSegment(sketch, "E765", {"start": v(-14.08, -6.43) * mm, "end": v(-14.07, -6.47) * mm});
            skLineSegment(sketch, "E766", {"start": v(-14.07, -6.47) * mm, "end": v(-14.06, -6.5) * mm});
            skLineSegment(sketch, "E767", {"start": v(-14.06, -6.5) * mm, "end": v(-14.04, -6.53) * mm});
            skLineSegment(sketch, "E768", {"start": v(-14.04, -6.53) * mm, "end": v(-14.03, -6.56) * mm});
            skLineSegment(sketch, "E769", {"start": v(-14.03, -6.56) * mm, "end": v(-14.02, -6.6) * mm});
            skLineSegment(sketch, "E770", {"start": v(-14.02, -6.6) * mm, "end": v(-14, -6.63) * mm});
            skLineSegment(sketch, "E771", {"start": v(-14, -6.63) * mm, "end": v(-14, -6.66) * mm});
            skLineSegment(sketch, "E772", {"start": v(-14, -6.66) * mm, "end": v(-13.98, -6.7) * mm});
            skLineSegment(sketch, "E773", {"start": v(-13.98, -6.7) * mm, "end": v(-13.97, -6.72) * mm});
            skLineSegment(sketch, "E774", {"start": v(-13.97, -6.72) * mm, "end": v(-13.65, -6.86) * mm});
            skLineSegment(sketch, "E775", {"start": v(-13.65, -6.86) * mm, "end": v(-13.33, -7) * mm});
            skLineSegment(sketch, "E776", {"start": v(-13.33, -7) * mm, "end": v(-13, -7.12) * mm});
            skLineSegment(sketch, "E777", {"start": v(-13, -7.12) * mm, "end": v(-12.69, -7.26) * mm});
            skLineSegment(sketch, "E778", {"start": v(-12.69, -7.26) * mm, "end": v(-12.37, -7.39) * mm});
            skLineSegment(sketch, "E779", {"start": v(-12.37, -7.39) * mm, "end": v(-12.05, -7.52) * mm});
            skLineSegment(sketch, "E780", {"start": v(-12.05, -7.52) * mm, "end": v(-11.73, -7.66) * mm});
            skLineSegment(sketch, "E781", {"start": v(-11.73, -7.66) * mm, "end": v(-11.4, -7.79) * mm});
            skLineSegment(sketch, "E782", {"start": v(-11.4, -7.79) * mm, "end": v(-11.1, -7.92) * mm});
            skLineSegment(sketch, "E783", {"start": v(-11.1, -7.92) * mm, "end": v(-10.77, -8.06) * mm});
            skLineSegment(sketch, "E784", {"start": v(-10.77, -8.06) * mm, "end": v(-10.45, -8.19) * mm});
            skLineSegment(sketch, "E785", {"start": v(-10.45, -8.19) * mm, "end": v(-10.13, -8.32) * mm});
            skLineSegment(sketch, "E786", {"start": v(-10.13, -8.32) * mm, "end": v(-9.81, -8.45) * mm});
            skLineSegment(sketch, "E787", {"start": v(-9.81, -8.45) * mm, "end": v(-9.5, -8.59) * mm});
            skLineSegment(sketch, "E788", {"start": v(-9.5, -8.59) * mm, "end": v(-9.17, -8.72) * mm});
            skLineSegment(sketch, "E789", {"start": v(-9.17, -8.72) * mm, "end": v(-8.85, -8.85) * mm});
            skLineSegment(sketch, "E790", {"start": v(-8.85, -8.85) * mm, "end": v(-8.72, -9.17) * mm});
            skLineSegment(sketch, "E791", {"start": v(-8.72, -9.17) * mm, "end": v(-8.59, -9.5) * mm});
            skLineSegment(sketch, "E792", {"start": v(-8.59, -9.5) * mm, "end": v(-8.45, -9.81) * mm});
            skLineSegment(sketch, "E793", {"start": v(-8.45, -9.81) * mm, "end": v(-8.32, -10.13) * mm});
            skLineSegment(sketch, "E794", {"start": v(-8.32, -10.13) * mm, "end": v(-8.19, -10.45) * mm});
            skLineSegment(sketch, "E795", {"start": v(-8.19, -10.45) * mm, "end": v(-8.06, -10.77) * mm});
            skLineSegment(sketch, "E796", {"start": v(-8.06, -10.77) * mm, "end": v(-7.92, -11.1) * mm});
            skLineSegment(sketch, "E797", {"start": v(-7.92, -11.1) * mm, "end": v(-7.79, -11.4) * mm});
            skLineSegment(sketch, "E798", {"start": v(-7.79, -11.4) * mm, "end": v(-7.66, -11.73) * mm});
            skLineSegment(sketch, "E799", {"start": v(-7.66, -11.73) * mm, "end": v(-7.52, -12.05) * mm});
            skLineSegment(sketch, "E800", {"start": v(-7.52, -12.05) * mm, "end": v(-7.39, -12.37) * mm});
            skLineSegment(sketch, "E801", {"start": v(-7.39, -12.37) * mm, "end": v(-7.26, -12.69) * mm});
            skLineSegment(sketch, "E802", {"start": v(-7.26, -12.69) * mm, "end": v(-7.12, -13) * mm});
            skLineSegment(sketch, "E803", {"start": v(-7.12, -13) * mm, "end": v(-7, -13.33) * mm});
            skLineSegment(sketch, "E804", {"start": v(-7, -13.33) * mm, "end": v(-6.86, -13.65) * mm});
            skLineSegment(sketch, "E805", {"start": v(-6.86, -13.65) * mm, "end": v(-6.72, -13.97) * mm});
            skLineSegment(sketch, "E806", {"start": v(-6.72, -13.97) * mm, "end": v(-6.7, -13.98) * mm});
            skLineSegment(sketch, "E807", {"start": v(-6.7, -13.98) * mm, "end": v(-6.66, -14) * mm});
            skLineSegment(sketch, "E808", {"start": v(-6.66, -14) * mm, "end": v(-6.63, -14) * mm});
            skLineSegment(sketch, "E809", {"start": v(-6.63, -14) * mm, "end": v(-6.6, -14.02) * mm});
            skLineSegment(sketch, "E810", {"start": v(-6.6, -14.02) * mm, "end": v(-6.56, -14.03) * mm});
            skLineSegment(sketch, "E811", {"start": v(-6.56, -14.03) * mm, "end": v(-6.53, -14.04) * mm});
            skLineSegment(sketch, "E812", {"start": v(-6.53, -14.04) * mm, "end": v(-6.5, -14.06) * mm});
            skLineSegment(sketch, "E813", {"start": v(-6.5, -14.06) * mm, "end": v(-6.47, -14.07) * mm});
            skLineSegment(sketch, "E814", {"start": v(-6.47, -14.07) * mm, "end": v(-6.43, -14.08) * mm});
            skLineSegment(sketch, "E815", {"start": v(-6.43, -14.08) * mm, "end": v(-6.4, -14.1) * mm});
            skLineSegment(sketch, "E816", {"start": v(-6.4, -14.1) * mm, "end": v(-6.37, -14.1) * mm});
            skLineSegment(sketch, "E817", {"start": v(-6.37, -14.1) * mm, "end": v(-6.34, -14.12) * mm});
            skLineSegment(sketch, "E818", {"start": v(-6.34, -14.12) * mm, "end": v(-6.3, -14.13) * mm});
            skLineSegment(sketch, "E819", {"start": v(-6.3, -14.13) * mm, "end": v(-6.27, -14.15) * mm});
            skLineSegment(sketch, "E820", {"start": v(-6.27, -14.15) * mm, "end": v(-6.24, -14.16) * mm});
            skLineSegment(sketch, "E821", {"start": v(-6.24, -14.16) * mm, "end": v(-6.2, -14.17) * mm});
            skLineSegment(sketch, "E822", {"start": v(-6.2, -14.17) * mm, "end": v(-6.08, -14.22) * mm});
            skLineSegment(sketch, "E823", {"start": v(-6.08, -14.22) * mm, "end": v(-5.95, -14.28) * mm});
            skLineSegment(sketch, "E824", {"start": v(-5.95, -14.28) * mm, "end": v(-5.82, -14.33) * mm});
            skLineSegment(sketch, "E825", {"start": v(-5.82, -14.33) * mm, "end": v(-5.69, -14.38) * mm});
            skLineSegment(sketch, "E826", {"start": v(-5.69, -14.38) * mm, "end": v(-5.56, -14.43) * mm});
            skLineSegment(sketch, "E827", {"start": v(-5.56, -14.43) * mm, "end": v(-5.43, -14.48) * mm});
            skLineSegment(sketch, "E828", {"start": v(-5.43, -14.48) * mm, "end": v(-5.3, -14.53) * mm});
            skLineSegment(sketch, "E829", {"start": v(-5.3, -14.53) * mm, "end": v(-5.17, -14.59) * mm});
            skLineSegment(sketch, "E830", {"start": v(-5.17, -14.59) * mm, "end": v(-5.04, -14.64) * mm});
            skLineSegment(sketch, "E831", {"start": v(-5.04, -14.64) * mm, "end": v(-4.91, -14.69) * mm});
            skLineSegment(sketch, "E832", {"start": v(-4.91, -14.69) * mm, "end": v(-4.78, -14.74) * mm});
            skLineSegment(sketch, "E833", {"start": v(-4.78, -14.74) * mm, "end": v(-4.66, -14.8) * mm});
            skLineSegment(sketch, "E834", {"start": v(-4.66, -14.8) * mm, "end": v(-4.53, -14.84) * mm});
            skLineSegment(sketch, "E835", {"start": v(-4.53, -14.84) * mm, "end": v(-4.4, -14.9) * mm});
            skLineSegment(sketch, "E836", {"start": v(-4.4, -14.9) * mm, "end": v(-4.27, -14.95) * mm});
            skLineSegment(sketch, "E837", {"start": v(-4.27, -14.95) * mm, "end": v(-4.14, -15) * mm});
            skLineSegment(sketch, "E838", {"start": v(-4.14, -15) * mm, "end": v(-4.14, -14.77) * mm});
            skLineSegment(sketch, "E839", {"start": v(-4.14, -14.77) * mm, "end": v(-4.14, -14.55) * mm});
            skLineSegment(sketch, "E840", {"start": v(-4.14, -14.55) * mm, "end": v(-4.14, -14.32) * mm});
            skLineSegment(sketch, "E841", {"start": v(-4.14, -14.32) * mm, "end": v(-4.14, -14.1) * mm});
            skLineSegment(sketch, "E842", {"start": v(-4.14, -14.1) * mm, "end": v(-4.14, -13.87) * mm});
            skLineSegment(sketch, "E843", {"start": v(-4.14, -13.87) * mm, "end": v(-4.14, -13.64) * mm});
            skLineSegment(sketch, "E844", {"start": v(-4.14, -13.64) * mm, "end": v(-4.14, -13.42) * mm});
            skLineSegment(sketch, "E845", {"start": v(-4.14, -13.42) * mm, "end": v(-4.14, -13.19) * mm});
            skLineSegment(sketch, "E846", {"start": v(-4.14, -13.19) * mm, "end": v(-4.14, -12.96) * mm});
            skLineSegment(sketch, "E847", {"start": v(-4.14, -12.96) * mm, "end": v(-4.14, -12.74) * mm});
            skLineSegment(sketch, "E848", {"start": v(-4.14, -12.74) * mm, "end": v(-4.14, -12.51) * mm});
            skLineSegment(sketch, "E849", {"start": v(-4.14, -12.51) * mm, "end": v(-4.14, -12.28) * mm});
            skLineSegment(sketch, "E850", {"start": v(-4.14, -12.28) * mm, "end": v(-4.14, -12.06) * mm});
            skLineSegment(sketch, "E851", {"start": v(-4.14, -12.06) * mm, "end": v(-4.14, -11.83) * mm});
            skLineSegment(sketch, "E852", {"start": v(-4.14, -11.83) * mm, "end": v(-4.14, -11.6) * mm});
            skLineSegment(sketch, "E853", {"start": v(-4.14, -11.6) * mm, "end": v(-4.14, -11.38) * mm});
            skLineSegment(sketch, "E854", {"start": v(-4.14, -11.38) * mm, "end": v(-4.14, -11.25) * mm});
            skLineSegment(sketch, "E855", {"start": v(-4.14, -11.25) * mm, "end": v(-4.14, -11.12) * mm});
            skLineSegment(sketch, "E856", {"start": v(-4.14, -11.12) * mm, "end": v(-4.14, -11) * mm});
            skLineSegment(sketch, "E857", {"start": v(-4.14, -11) * mm, "end": v(-4.14, -10.86) * mm});
            skLineSegment(sketch, "E858", {"start": v(-4.14, -10.86) * mm, "end": v(-4.14, -10.73) * mm});
            skLineSegment(sketch, "E859", {"start": v(-4.14, -10.73) * mm, "end": v(-4.14, -10.6) * mm});
            skLineSegment(sketch, "E860", {"start": v(-4.14, -10.6) * mm, "end": v(-4.14, -10.47) * mm});
            skLineSegment(sketch, "E861", {"start": v(-4.14, -10.47) * mm, "end": v(-4.14, -10.34) * mm});
            skLineSegment(sketch, "E862", {"start": v(-4.14, -10.34) * mm, "end": v(-4.14, -10.22) * mm});
            skLineSegment(sketch, "E863", {"start": v(-4.14, -10.22) * mm, "end": v(-4.14, -10.09) * mm});
            skLineSegment(sketch, "E864", {"start": v(-4.14, -10.09) * mm, "end": v(-4.14, -9.96) * mm});
            skLineSegment(sketch, "E865", {"start": v(-4.14, -9.96) * mm, "end": v(-4.14, -9.83) * mm});
            skLineSegment(sketch, "E866", {"start": v(-4.14, -9.83) * mm, "end": v(-4.14, -9.7) * mm});
            skLineSegment(sketch, "E867", {"start": v(-4.14, -9.7) * mm, "end": v(-4.14, -9.57) * mm});
            skLineSegment(sketch, "E868", {"start": v(-4.14, -9.57) * mm, "end": v(-4.14, -9.44) * mm});
            skLineSegment(sketch, "E869", {"start": v(-4.14, -9.44) * mm, "end": v(-4.14, -9.31) * mm});
            skLineSegment(sketch, "E870", {"start": v(-4.14, -9.31) * mm, "end": v(-4.02, -9.31) * mm});
            skLineSegment(sketch, "E871", {"start": v(-4.02, -9.31) * mm, "end": v(-3.91, -9.31) * mm});
            skLineSegment(sketch, "E872", {"start": v(-3.91, -9.31) * mm, "end": v(-3.8, -9.31) * mm});
            skLineSegment(sketch, "E873", {"start": v(-3.8, -9.31) * mm, "end": v(-3.69, -9.31) * mm});
            skLineSegment(sketch, "E874", {"start": v(-3.69, -9.31) * mm, "end": v(-3.57, -9.31) * mm});
            skLineSegment(sketch, "E875", {"start": v(-3.57, -9.31) * mm, "end": v(-3.46, -9.31) * mm});
            skLineSegment(sketch, "E876", {"start": v(-3.46, -9.31) * mm, "end": v(-3.35, -9.31) * mm});
            skLineSegment(sketch, "E877", {"start": v(-3.35, -9.31) * mm, "end": v(-3.23, -9.31) * mm});
            skLineSegment(sketch, "E878", {"start": v(-3.23, -9.31) * mm, "end": v(-3.12, -9.31) * mm});
            skLineSegment(sketch, "E879", {"start": v(-3.12, -9.31) * mm, "end": v(-3, -9.31) * mm});
            skLineSegment(sketch, "E880", {"start": v(-3, -9.31) * mm, "end": v(-2.9, -9.31) * mm});
            skLineSegment(sketch, "E881", {"start": v(-2.9, -9.31) * mm, "end": v(-2.78, -9.31) * mm});
            skLineSegment(sketch, "E882", {"start": v(-2.78, -9.31) * mm, "end": v(-2.67, -9.31) * mm});
            skLineSegment(sketch, "E883", {"start": v(-2.67, -9.31) * mm, "end": v(-2.55, -9.31) * mm});
            skLineSegment(sketch, "E884", {"start": v(-2.55, -9.31) * mm, "end": v(-2.44, -9.31) * mm});
            skLineSegment(sketch, "E885", {"start": v(-2.44, -9.31) * mm, "end": v(-2.33, -9.31) * mm});
            skLineSegment(sketch, "E886", {"start": v(-2.33, -9.31) * mm, "end": v(-2.2, -9.3) * mm});
            skLineSegment(sketch, "E887", {"start": v(-2.2, -9.3) * mm, "end": v(-2.07, -9.28) * mm});
            skLineSegment(sketch, "E888", {"start": v(-2.07, -9.28) * mm, "end": v(-1.94, -9.25) * mm});
            skLineSegment(sketch, "E889", {"start": v(-1.94, -9.25) * mm, "end": v(-1.82, -9.2) * mm});
            skLineSegment(sketch, "E890", {"start": v(-1.82, -9.2) * mm, "end": v(-1.71, -9.15) * mm});
            skLineSegment(sketch, "E891", {"start": v(-1.71, -9.15) * mm, "end": v(-1.6, -9.09) * mm});
            skLineSegment(sketch, "E892", {"start": v(-1.6, -9.09) * mm, "end": v(-1.5, -9.02) * mm});
            skLineSegment(sketch, "E893", {"start": v(-1.5, -9.02) * mm, "end": v(-1.41, -8.93) * mm});
            skLineSegment(sketch, "E894", {"start": v(-1.41, -8.93) * mm, "end": v(-1.33, -8.84) * mm});
            skLineSegment(sketch, "E895", {"start": v(-1.33, -8.84) * mm, "end": v(-1.26, -8.74) * mm});
            skLineSegment(sketch, "E896", {"start": v(-1.26, -8.74) * mm, "end": v(-1.2, -8.63) * mm});
            skLineSegment(sketch, "E897", {"start": v(-1.2, -8.63) * mm, "end": v(-1.14, -8.52) * mm});
            skLineSegment(sketch, "E898", {"start": v(-1.14, -8.52) * mm, "end": v(-1.1, -8.4) * mm});
            skLineSegment(sketch, "E899", {"start": v(-1.1, -8.4) * mm, "end": v(-1.06, -8.28) * mm});
            skLineSegment(sketch, "E900", {"start": v(-1.06, -8.28) * mm, "end": v(-1.04, -8.15) * mm});
            skLineSegment(sketch, "E901", {"start": v(-1.04, -8.15) * mm, "end": v(-1.03, -8.02) * mm});
            skLineSegment(sketch, "E902", {"start": v(-1.03, -8.02) * mm, "end": v(-1.03, -7.9) * mm});
            skLineSegment(sketch, "E903", {"start": v(-1.03, -7.9) * mm, "end": v(-1.03, -7.8) * mm});
            skLineSegment(sketch, "E904", {"start": v(-1.03, -7.8) * mm, "end": v(-1.03, -7.68) * mm});
            skLineSegment(sketch, "E905", {"start": v(-1.03, -7.68) * mm, "end": v(-1.03, -7.56) * mm});
            skLineSegment(sketch, "E906", {"start": v(-1.03, -7.56) * mm, "end": v(-1.03, -7.45) * mm});
            skLineSegment(sketch, "E907", {"start": v(-1.03, -7.45) * mm, "end": v(-1.03, -7.34) * mm});
            skLineSegment(sketch, "E908", {"start": v(-1.03, -7.34) * mm, "end": v(-1.03, -7.23) * mm});
            skLineSegment(sketch, "E909", {"start": v(-1.03, -7.23) * mm, "end": v(-1.03, -7.11) * mm});
            skLineSegment(sketch, "E910", {"start": v(-1.03, -7.11) * mm, "end": v(-1.03, -7) * mm});
            skLineSegment(sketch, "E911", {"start": v(-1.03, -7) * mm, "end": v(-1.03, -6.89) * mm});
            skLineSegment(sketch, "E912", {"start": v(-1.03, -6.89) * mm, "end": v(-1.03, -6.77) * mm});
            skLineSegment(sketch, "E913", {"start": v(-1.03, -6.77) * mm, "end": v(-1.03, -6.66) * mm});
            skLineSegment(sketch, "E914", {"start": v(-1.03, -6.66) * mm, "end": v(-1.03, -6.55) * mm});
            skLineSegment(sketch, "E915", {"start": v(-1.03, -6.55) * mm, "end": v(-1.03, -6.43) * mm});
            skLineSegment(sketch, "E916", {"start": v(-1.03, -6.43) * mm, "end": v(-1.03, -6.32) * mm});
            skLineSegment(sketch, "E917", {"start": v(-1.03, -6.32) * mm, "end": v(-1.03, -6.2) * mm});
            skLineSegment(sketch, "E918", {"start": v(-1.03, -6.2) * mm, "end": v(-0.97, -6.2) * mm});
            skLineSegment(sketch, "E919", {"start": v(-0.97, -6.2) * mm, "end": v(-0.9, -6.2) * mm});
            skLineSegment(sketch, "E920", {"start": v(-0.9, -6.2) * mm, "end": v(-0.84, -6.2) * mm});
            skLineSegment(sketch, "E921", {"start": v(-0.84, -6.2) * mm, "end": v(-0.78, -6.2) * mm});
            skLineSegment(sketch, "E922", {"start": v(-0.78, -6.2) * mm, "end": v(-0.71, -6.2) * mm});
            skLineSegment(sketch, "E923", {"start": v(-0.71, -6.2) * mm, "end": v(-0.65, -6.2) * mm});
            skLineSegment(sketch, "E924", {"start": v(-0.65, -6.2) * mm, "end": v(-0.58, -6.2) * mm});
            skLineSegment(sketch, "E925", {"start": v(-0.58, -6.2) * mm, "end": v(-0.52, -6.2) * mm});
            skLineSegment(sketch, "E926", {"start": v(-0.52, -6.2) * mm, "end": v(-0.45, -6.2) * mm});
            skLineSegment(sketch, "E927", {"start": v(-0.45, -6.2) * mm, "end": v(-0.39, -6.2) * mm});
            skLineSegment(sketch, "E928", {"start": v(-0.39, -6.2) * mm, "end": v(-0.32, -6.2) * mm});
            skLineSegment(sketch, "E929", {"start": v(-0.32, -6.2) * mm, "end": v(-0.26, -6.2) * mm});
            skLineSegment(sketch, "E930", {"start": v(-0.26, -6.2) * mm, "end": v(-0.2, -6.2) * mm});
            skLineSegment(sketch, "E931", {"start": v(-0.2, -6.2) * mm, "end": v(-0.13, -6.2) * mm});
            skLineSegment(sketch, "E932", {"start": v(-0.13, -6.2) * mm, "end": v(-0.06, -6.2) * mm});
            skLineSegment(sketch, "E933", {"start": v(-0.06, -6.2) * mm, "end": v(0, -6.2) * mm});
            skLineSegment(sketch, "E934", {"start": v(0, -6.2) * mm, "end": v(0.06, -6.2) * mm});
            skLineSegment(sketch, "E935", {"start": v(0.06, -6.2) * mm, "end": v(0.13, -6.2) * mm});
            skLineSegment(sketch, "E936", {"start": v(0.13, -6.2) * mm, "end": v(0.2, -6.2) * mm});
            skLineSegment(sketch, "E937", {"start": v(0.2, -6.2) * mm, "end": v(0.26, -6.2) * mm});
            skLineSegment(sketch, "E938", {"start": v(0.26, -6.2) * mm, "end": v(0.32, -6.2) * mm});
            skLineSegment(sketch, "E939", {"start": v(0.32, -6.2) * mm, "end": v(0.39, -6.2) * mm});
            skLineSegment(sketch, "E940", {"start": v(0.39, -6.2) * mm, "end": v(0.45, -6.2) * mm});
            skLineSegment(sketch, "E941", {"start": v(0.45, -6.2) * mm, "end": v(0.52, -6.2) * mm});
            skLineSegment(sketch, "E942", {"start": v(0.52, -6.2) * mm, "end": v(0.58, -6.2) * mm});
            skLineSegment(sketch, "E943", {"start": v(0.58, -6.2) * mm, "end": v(0.65, -6.2) * mm});
            skLineSegment(sketch, "E944", {"start": v(0.65, -6.2) * mm, "end": v(0.71, -6.2) * mm});
            skLineSegment(sketch, "E945", {"start": v(0.71, -6.2) * mm, "end": v(0.78, -6.2) * mm});
            skLineSegment(sketch, "E946", {"start": v(0.78, -6.2) * mm, "end": v(0.84, -6.2) * mm});
            skLineSegment(sketch, "E947", {"start": v(0.84, -6.2) * mm, "end": v(0.9, -6.2) * mm});
            skLineSegment(sketch, "E948", {"start": v(0.9, -6.2) * mm, "end": v(0.97, -6.2) * mm});
            skLineSegment(sketch, "E949", {"start": v(0.97, -6.2) * mm, "end": v(1.03, -6.2) * mm});
            skLineSegment(sketch, "E950", {"start": v(1.03, -6.2) * mm, "end": v(1.03, -6.32) * mm});
            skLineSegment(sketch, "E951", {"start": v(1.03, -6.32) * mm, "end": v(1.03, -6.43) * mm});
            skLineSegment(sketch, "E952", {"start": v(1.03, -6.43) * mm, "end": v(1.03, -6.55) * mm});
            skLineSegment(sketch, "E953", {"start": v(1.03, -6.55) * mm, "end": v(1.03, -6.66) * mm});
            skLineSegment(sketch, "E954", {"start": v(1.03, -6.66) * mm, "end": v(1.03, -6.77) * mm});
            skLineSegment(sketch, "E955", {"start": v(1.03, -6.77) * mm, "end": v(1.03, -6.89) * mm});
            skLineSegment(sketch, "E956", {"start": v(1.03, -6.89) * mm, "end": v(1.03, -7) * mm});
            skLineSegment(sketch, "E957", {"start": v(1.03, -7) * mm, "end": v(1.03, -7.11) * mm});
            skLineSegment(sketch, "E958", {"start": v(1.03, -7.11) * mm, "end": v(1.03, -7.23) * mm});
            skLineSegment(sketch, "E959", {"start": v(1.03, -7.23) * mm, "end": v(1.03, -7.34) * mm});
            skLineSegment(sketch, "E960", {"start": v(1.03, -7.34) * mm, "end": v(1.03, -7.45) * mm});
            skLineSegment(sketch, "E961", {"start": v(1.03, -7.45) * mm, "end": v(1.03, -7.56) * mm});
            skLineSegment(sketch, "E962", {"start": v(1.03, -7.56) * mm, "end": v(1.03, -7.68) * mm});
            skLineSegment(sketch, "E963", {"start": v(1.03, -7.68) * mm, "end": v(1.03, -7.8) * mm});
            skLineSegment(sketch, "E964", {"start": v(1.03, -7.8) * mm, "end": v(1.03, -7.9) * mm});
            skLineSegment(sketch, "E965", {"start": v(1.03, -7.9) * mm, "end": v(1.03, -8.02) * mm});
            skLineSegment(sketch, "E966", {"start": v(1.03, -8.02) * mm, "end": v(1.04, -8.15) * mm});
            skLineSegment(sketch, "E967", {"start": v(1.04, -8.15) * mm, "end": v(1.06, -8.28) * mm});
            skLineSegment(sketch, "E968", {"start": v(1.06, -8.28) * mm, "end": v(1.1, -8.4) * mm});
            skLineSegment(sketch, "E969", {"start": v(1.1, -8.4) * mm, "end": v(1.14, -8.52) * mm});
            skLineSegment(sketch, "E970", {"start": v(1.14, -8.52) * mm, "end": v(1.2, -8.63) * mm});
            skLineSegment(sketch, "E971", {"start": v(1.2, -8.63) * mm, "end": v(1.26, -8.74) * mm});
            skLineSegment(sketch, "E972", {"start": v(1.26, -8.74) * mm, "end": v(1.33, -8.84) * mm});
            skLineSegment(sketch, "E973", {"start": v(1.33, -8.84) * mm, "end": v(1.41, -8.93) * mm});
            skLineSegment(sketch, "E974", {"start": v(1.41, -8.93) * mm, "end": v(1.5, -9.02) * mm});
            skLineSegment(sketch, "E975", {"start": v(1.5, -9.02) * mm, "end": v(1.6, -9.09) * mm});
            skLineSegment(sketch, "E976", {"start": v(1.6, -9.09) * mm, "end": v(1.71, -9.15) * mm});
            skLineSegment(sketch, "E977", {"start": v(1.71, -9.15) * mm, "end": v(1.82, -9.2) * mm});
            skLineSegment(sketch, "E978", {"start": v(1.82, -9.2) * mm, "end": v(1.94, -9.25) * mm});
            skLineSegment(sketch, "E979", {"start": v(1.94, -9.25) * mm, "end": v(2.07, -9.28) * mm});
            skLineSegment(sketch, "E980", {"start": v(2.07, -9.28) * mm, "end": v(2.2, -9.3) * mm});
            skLineSegment(sketch, "E981", {"start": v(2.2, -9.3) * mm, "end": v(2.33, -9.31) * mm});
            skLineSegment(sketch, "E982", {"start": v(2.33, -9.31) * mm, "end": v(2.44, -9.31) * mm});
            skLineSegment(sketch, "E983", {"start": v(2.44, -9.31) * mm, "end": v(2.55, -9.31) * mm});
            skLineSegment(sketch, "E984", {"start": v(2.55, -9.31) * mm, "end": v(2.67, -9.31) * mm});
            skLineSegment(sketch, "E985", {"start": v(2.67, -9.31) * mm, "end": v(2.78, -9.31) * mm});
            skLineSegment(sketch, "E986", {"start": v(2.78, -9.31) * mm, "end": v(2.9, -9.31) * mm});
            skLineSegment(sketch, "E987", {"start": v(2.9, -9.31) * mm, "end": v(3, -9.31) * mm});
            skLineSegment(sketch, "E988", {"start": v(3, -9.31) * mm, "end": v(3.12, -9.31) * mm});
            skLineSegment(sketch, "E989", {"start": v(3.12, -9.31) * mm, "end": v(3.23, -9.31) * mm});
            skLineSegment(sketch, "E990", {"start": v(3.23, -9.31) * mm, "end": v(3.35, -9.31) * mm});
            skLineSegment(sketch, "E991", {"start": v(3.35, -9.31) * mm, "end": v(3.46, -9.31) * mm});
            skLineSegment(sketch, "E992", {"start": v(3.46, -9.31) * mm, "end": v(3.57, -9.31) * mm});
            skLineSegment(sketch, "E993", {"start": v(3.57, -9.31) * mm, "end": v(3.69, -9.31) * mm});
            skLineSegment(sketch, "E994", {"start": v(3.69, -9.31) * mm, "end": v(3.8, -9.31) * mm});
            skLineSegment(sketch, "E995", {"start": v(3.8, -9.31) * mm, "end": v(3.91, -9.31) * mm});
            skLineSegment(sketch, "E996", {"start": v(3.91, -9.31) * mm, "end": v(4.02, -9.31) * mm});
            skLineSegment(sketch, "E997", {"start": v(4.02, -9.31) * mm, "end": v(4.14, -9.31) * mm});
            skLineSegment(sketch, "E998", {"start": v(4.14, -9.31) * mm, "end": v(4.14, -9.44) * mm});
            skLineSegment(sketch, "E999", {"start": v(4.14, -9.44) * mm, "end": v(4.14, -9.57) * mm});
            skLineSegment(sketch, "E1000", {"start": v(4.14, -9.57) * mm, "end": v(4.14, -9.7) * mm});
            skLineSegment(sketch, "E1001", {"start": v(4.14, -9.7) * mm, "end": v(4.14, -9.83) * mm});
            skLineSegment(sketch, "E1002", {"start": v(4.14, -9.83) * mm, "end": v(4.14, -9.96) * mm});
            skLineSegment(sketch, "E1003", {"start": v(4.14, -9.96) * mm, "end": v(4.14, -10.09) * mm});
            skLineSegment(sketch, "E1004", {"start": v(4.14, -10.09) * mm, "end": v(4.14, -10.22) * mm});
            skLineSegment(sketch, "E1005", {"start": v(4.14, -10.22) * mm, "end": v(4.14, -10.34) * mm});
            skLineSegment(sketch, "E1006", {"start": v(4.14, -10.34) * mm, "end": v(4.14, -10.47) * mm});
            skLineSegment(sketch, "E1007", {"start": v(4.14, -10.47) * mm, "end": v(4.14, -10.6) * mm});
            skLineSegment(sketch, "E1008", {"start": v(4.14, -10.6) * mm, "end": v(4.14, -10.73) * mm});
            skLineSegment(sketch, "E1009", {"start": v(4.14, -10.73) * mm, "end": v(4.14, -10.86) * mm});
            skLineSegment(sketch, "E1010", {"start": v(4.14, -10.86) * mm, "end": v(4.14, -11) * mm});
            skLineSegment(sketch, "E1011", {"start": v(4.14, -11) * mm, "end": v(4.14, -11.12) * mm});
            skLineSegment(sketch, "E1012", {"start": v(4.14, -11.12) * mm, "end": v(4.14, -11.25) * mm});
            skLineSegment(sketch, "E1013", {"start": v(4.14, -11.25) * mm, "end": v(4.14, -11.38) * mm});
            skLineSegment(sketch, "E1014", {"start": v(4.14, -11.38) * mm, "end": v(4.14, -11.6) * mm});
            skLineSegment(sketch, "E1015", {"start": v(4.14, -11.6) * mm, "end": v(4.14, -11.83) * mm});
            skLineSegment(sketch, "E1016", {"start": v(4.14, -11.83) * mm, "end": v(4.14, -12.06) * mm});
            skLineSegment(sketch, "E1017", {"start": v(4.14, -12.06) * mm, "end": v(4.14, -12.28) * mm});
            skLineSegment(sketch, "E1018", {"start": v(4.14, -12.28) * mm, "end": v(4.14, -12.51) * mm});
            skLineSegment(sketch, "E1019", {"start": v(4.14, -12.51) * mm, "end": v(4.14, -12.74) * mm});
            skLineSegment(sketch, "E1020", {"start": v(4.14, -12.74) * mm, "end": v(4.14, -12.96) * mm});
            skLineSegment(sketch, "E1021", {"start": v(4.14, -12.96) * mm, "end": v(4.14, -13.19) * mm});
            skLineSegment(sketch, "E1022", {"start": v(4.14, -13.19) * mm, "end": v(4.14, -13.42) * mm});
            skLineSegment(sketch, "E1023", {"start": v(4.14, -13.42) * mm, "end": v(4.14, -13.64) * mm});
            skLineSegment(sketch, "E1024", {"start": v(4.14, -13.64) * mm, "end": v(4.14, -13.87) * mm});
            skLineSegment(sketch, "E1025", {"start": v(4.14, -13.87) * mm, "end": v(4.14, -14.1) * mm});
            skLineSegment(sketch, "E1026", {"start": v(4.14, -14.1) * mm, "end": v(4.14, -14.32) * mm});
            skLineSegment(sketch, "E1027", {"start": v(4.14, -14.32) * mm, "end": v(4.14, -14.55) * mm});
            skLineSegment(sketch, "E1028", {"start": v(4.14, -14.55) * mm, "end": v(4.14, -14.77) * mm});
            skLineSegment(sketch, "E1029", {"start": v(4.14, -14.77) * mm, "end": v(4.14, -15) * mm});
            skLineSegment(sketch, "E1030", {"start": v(4.14, -15) * mm, "end": v(4.27, -14.95) * mm});
            skLineSegment(sketch, "E1031", {"start": v(4.27, -14.95) * mm, "end": v(4.4, -14.9) * mm});
            skLineSegment(sketch, "E1032", {"start": v(4.4, -14.9) * mm, "end": v(4.53, -14.84) * mm});
            skLineSegment(sketch, "E1033", {"start": v(4.53, -14.84) * mm, "end": v(4.66, -14.8) * mm});
            skLineSegment(sketch, "E1034", {"start": v(4.66, -14.8) * mm, "end": v(4.78, -14.74) * mm});
            skLineSegment(sketch, "E1035", {"start": v(4.78, -14.74) * mm, "end": v(4.91, -14.69) * mm});
            skLineSegment(sketch, "E1036", {"start": v(4.91, -14.69) * mm, "end": v(5.04, -14.64) * mm});
            skLineSegment(sketch, "E1037", {"start": v(5.04, -14.64) * mm, "end": v(5.17, -14.59) * mm});
            skLineSegment(sketch, "E1038", {"start": v(5.17, -14.59) * mm, "end": v(5.3, -14.53) * mm});
            skLineSegment(sketch, "E1039", {"start": v(5.3, -14.53) * mm, "end": v(5.43, -14.48) * mm});
            skLineSegment(sketch, "E1040", {"start": v(5.43, -14.48) * mm, "end": v(5.56, -14.43) * mm});
            skLineSegment(sketch, "E1041", {"start": v(5.56, -14.43) * mm, "end": v(5.69, -14.38) * mm});
            skLineSegment(sketch, "E1042", {"start": v(5.69, -14.38) * mm, "end": v(5.82, -14.33) * mm});
            skLineSegment(sketch, "E1043", {"start": v(5.82, -14.33) * mm, "end": v(5.95, -14.28) * mm});
            skLineSegment(sketch, "E1044", {"start": v(5.95, -14.28) * mm, "end": v(6.08, -14.22) * mm});
            skLineSegment(sketch, "E1045", {"start": v(6.08, -14.22) * mm, "end": v(6.2, -14.17) * mm});
            skLineSegment(sketch, "E1046", {"start": v(6.2, -14.17) * mm, "end": v(6.24, -14.16) * mm});
            skLineSegment(sketch, "E1047", {"start": v(6.24, -14.16) * mm, "end": v(6.27, -14.15) * mm});
            skLineSegment(sketch, "E1048", {"start": v(6.27, -14.15) * mm, "end": v(6.3, -14.13) * mm});
            skLineSegment(sketch, "E1049", {"start": v(6.3, -14.13) * mm, "end": v(6.34, -14.12) * mm});
            skLineSegment(sketch, "E1050", {"start": v(6.34, -14.12) * mm, "end": v(6.37, -14.1) * mm});
            skLineSegment(sketch, "E1051", {"start": v(6.37, -14.1) * mm, "end": v(6.4, -14.1) * mm});
            skLineSegment(sketch, "E1052", {"start": v(6.4, -14.1) * mm, "end": v(6.43, -14.08) * mm});
            skLineSegment(sketch, "E1053", {"start": v(6.43, -14.08) * mm, "end": v(6.47, -14.07) * mm});
            skLineSegment(sketch, "E1054", {"start": v(6.47, -14.07) * mm, "end": v(6.5, -14.06) * mm});
            skLineSegment(sketch, "E1055", {"start": v(6.5, -14.06) * mm, "end": v(6.53, -14.04) * mm});
            skLineSegment(sketch, "E1056", {"start": v(6.53, -14.04) * mm, "end": v(6.56, -14.03) * mm});
            skLineSegment(sketch, "E1057", {"start": v(6.56, -14.03) * mm, "end": v(6.6, -14.02) * mm});
            skLineSegment(sketch, "E1058", {"start": v(6.6, -14.02) * mm, "end": v(6.63, -14) * mm});
            skLineSegment(sketch, "E1059", {"start": v(6.63, -14) * mm, "end": v(6.66, -14) * mm});
            skLineSegment(sketch, "E1060", {"start": v(6.66, -14) * mm, "end": v(6.7, -13.98) * mm});
            skLineSegment(sketch, "E1061", {"start": v(6.7, -13.98) * mm, "end": v(6.72, -13.97) * mm});
            skLineSegment(sketch, "E1062", {"start": v(6.72, -13.97) * mm, "end": v(6.86, -13.65) * mm});
            skLineSegment(sketch, "E1063", {"start": v(6.86, -13.65) * mm, "end": v(7, -13.33) * mm});
            skLineSegment(sketch, "E1064", {"start": v(7, -13.33) * mm, "end": v(7.12, -13) * mm});
            skLineSegment(sketch, "E1065", {"start": v(7.12, -13) * mm, "end": v(7.26, -12.69) * mm});
            skLineSegment(sketch, "E1066", {"start": v(7.26, -12.69) * mm, "end": v(7.39, -12.37) * mm});
            skLineSegment(sketch, "E1067", {"start": v(7.39, -12.37) * mm, "end": v(7.52, -12.05) * mm});
            skLineSegment(sketch, "E1068", {"start": v(7.52, -12.05) * mm, "end": v(7.66, -11.73) * mm});
            skLineSegment(sketch, "E1069", {"start": v(7.66, -11.73) * mm, "end": v(7.79, -11.4) * mm});
            skLineSegment(sketch, "E1070", {"start": v(7.79, -11.4) * mm, "end": v(7.92, -11.1) * mm});
            skLineSegment(sketch, "E1071", {"start": v(7.92, -11.1) * mm, "end": v(8.06, -10.77) * mm});
            skLineSegment(sketch, "E1072", {"start": v(8.06, -10.77) * mm, "end": v(8.19, -10.45) * mm});
            skLineSegment(sketch, "E1073", {"start": v(8.19, -10.45) * mm, "end": v(8.32, -10.13) * mm});
            skLineSegment(sketch, "E1074", {"start": v(8.32, -10.13) * mm, "end": v(8.45, -9.81) * mm});
            skLineSegment(sketch, "E1075", {"start": v(8.45, -9.81) * mm, "end": v(8.59, -9.5) * mm});
            skLineSegment(sketch, "E1076", {"start": v(8.59, -9.5) * mm, "end": v(8.72, -9.17) * mm});
            skLineSegment(sketch, "E1077", {"start": v(8.72, -9.17) * mm, "end": v(8.85, -8.85) * mm});
            skLineSegment(sketch, "E1078", {"start": v(8.85, -8.85) * mm, "end": v(9.17, -8.72) * mm});
            skLineSegment(sketch, "E1079", {"start": v(9.17, -8.72) * mm, "end": v(9.5, -8.59) * mm});
            skLineSegment(sketch, "E1080", {"start": v(9.5, -8.59) * mm, "end": v(9.81, -8.45) * mm});
            skLineSegment(sketch, "E1081", {"start": v(9.81, -8.45) * mm, "end": v(10.13, -8.32) * mm});
            skLineSegment(sketch, "E1082", {"start": v(10.13, -8.32) * mm, "end": v(10.45, -8.19) * mm});
            skLineSegment(sketch, "E1083", {"start": v(10.45, -8.19) * mm, "end": v(10.77, -8.06) * mm});
            skLineSegment(sketch, "E1084", {"start": v(10.77, -8.06) * mm, "end": v(11.1, -7.92) * mm});
            skLineSegment(sketch, "E1085", {"start": v(11.1, -7.92) * mm, "end": v(11.4, -7.79) * mm});
            skLineSegment(sketch, "E1086", {"start": v(11.4, -7.79) * mm, "end": v(11.73, -7.66) * mm});
            skLineSegment(sketch, "E1087", {"start": v(11.73, -7.66) * mm, "end": v(12.05, -7.52) * mm});
            skLineSegment(sketch, "E1088", {"start": v(12.05, -7.52) * mm, "end": v(12.37, -7.39) * mm});
            skLineSegment(sketch, "E1089", {"start": v(12.37, -7.39) * mm, "end": v(12.69, -7.26) * mm});
            skLineSegment(sketch, "E1090", {"start": v(12.69, -7.26) * mm, "end": v(13, -7.12) * mm});
            skLineSegment(sketch, "E1091", {"start": v(13, -7.12) * mm, "end": v(13.33, -7) * mm});
            skLineSegment(sketch, "E1092", {"start": v(13.33, -7) * mm, "end": v(13.65, -6.86) * mm});
            skLineSegment(sketch, "E1093", {"start": v(13.65, -6.86) * mm, "end": v(13.97, -6.72) * mm});
            skLineSegment(sketch, "E1094", {"start": v(13.97, -6.72) * mm, "end": v(13.98, -6.7) * mm});
            skLineSegment(sketch, "E1095", {"start": v(13.98, -6.7) * mm, "end": v(14, -6.66) * mm});
            skLineSegment(sketch, "E1096", {"start": v(14, -6.66) * mm, "end": v(14, -6.63) * mm});
            skLineSegment(sketch, "E1097", {"start": v(14, -6.63) * mm, "end": v(14.02, -6.6) * mm});
            skLineSegment(sketch, "E1098", {"start": v(14.02, -6.6) * mm, "end": v(14.03, -6.56) * mm});
            skLineSegment(sketch, "E1099", {"start": v(14.03, -6.56) * mm, "end": v(14.04, -6.53) * mm});
            skLineSegment(sketch, "E1100", {"start": v(14.04, -6.53) * mm, "end": v(14.06, -6.5) * mm});
            skLineSegment(sketch, "E1101", {"start": v(14.06, -6.5) * mm, "end": v(14.07, -6.47) * mm});
            skLineSegment(sketch, "E1102", {"start": v(14.07, -6.47) * mm, "end": v(14.08, -6.43) * mm});
            skLineSegment(sketch, "E1103", {"start": v(14.08, -6.43) * mm, "end": v(14.1, -6.4) * mm});
            skLineSegment(sketch, "E1104", {"start": v(14.1, -6.4) * mm, "end": v(14.1, -6.37) * mm});
            skLineSegment(sketch, "E1105", {"start": v(14.1, -6.37) * mm, "end": v(14.12, -6.34) * mm});
            skLineSegment(sketch, "E1106", {"start": v(14.12, -6.34) * mm, "end": v(14.13, -6.3) * mm});
            skLineSegment(sketch, "E1107", {"start": v(14.13, -6.3) * mm, "end": v(14.15, -6.27) * mm});
            skLineSegment(sketch, "E1108", {"start": v(14.15, -6.27) * mm, "end": v(14.16, -6.24) * mm});
            skLineSegment(sketch, "E1109", {"start": v(14.16, -6.24) * mm, "end": v(14.17, -6.2) * mm});
            skLineSegment(sketch, "E1110", {"start": v(14.17, -6.2) * mm, "end": v(14.22, -6.08) * mm});
            skLineSegment(sketch, "E1111", {"start": v(14.22, -6.08) * mm, "end": v(14.28, -5.95) * mm});
            skLineSegment(sketch, "E1112", {"start": v(14.28, -5.95) * mm, "end": v(14.33, -5.82) * mm});
            skLineSegment(sketch, "E1113", {"start": v(14.33, -5.82) * mm, "end": v(14.38, -5.69) * mm});
            skLineSegment(sketch, "E1114", {"start": v(14.38, -5.69) * mm, "end": v(14.43, -5.56) * mm});
            skLineSegment(sketch, "E1115", {"start": v(14.43, -5.56) * mm, "end": v(14.48, -5.43) * mm});
            skLineSegment(sketch, "E1116", {"start": v(14.48, -5.43) * mm, "end": v(14.53, -5.3) * mm});
            skLineSegment(sketch, "E1117", {"start": v(14.53, -5.3) * mm, "end": v(14.59, -5.17) * mm});
            skLineSegment(sketch, "E1118", {"start": v(14.59, -5.17) * mm, "end": v(14.64, -5.04) * mm});
            skLineSegment(sketch, "E1119", {"start": v(14.64, -5.04) * mm, "end": v(14.69, -4.91) * mm});
            skLineSegment(sketch, "E1120", {"start": v(14.69, -4.91) * mm, "end": v(14.74, -4.78) * mm});
            skLineSegment(sketch, "E1121", {"start": v(14.74, -4.78) * mm, "end": v(14.8, -4.66) * mm});
            skLineSegment(sketch, "E1122", {"start": v(14.8, -4.66) * mm, "end": v(14.84, -4.53) * mm});
            skLineSegment(sketch, "E1123", {"start": v(14.84, -4.53) * mm, "end": v(14.9, -4.4) * mm});
            skLineSegment(sketch, "E1124", {"start": v(14.9, -4.4) * mm, "end": v(14.95, -4.27) * mm});
            skLineSegment(sketch, "E1125", {"start": v(14.95, -4.27) * mm, "end": v(15, -4.14) * mm});
            skLineSegment(sketch, "E1126", {"start": v(15, -4.14) * mm, "end": v(14.77, -4.14) * mm});
            skLineSegment(sketch, "E1127", {"start": v(14.77, -4.14) * mm, "end": v(14.55, -4.14) * mm});
            skLineSegment(sketch, "E1128", {"start": v(14.55, -4.14) * mm, "end": v(14.32, -4.14) * mm});
            skLineSegment(sketch, "E1129", {"start": v(14.32, -4.14) * mm, "end": v(14.1, -4.14) * mm});
            skLineSegment(sketch, "E1130", {"start": v(14.1, -4.14) * mm, "end": v(13.87, -4.14) * mm});
            skLineSegment(sketch, "E1131", {"start": v(13.87, -4.14) * mm, "end": v(13.64, -4.14) * mm});
            skLineSegment(sketch, "E1132", {"start": v(13.64, -4.14) * mm, "end": v(13.42, -4.14) * mm});
            skLineSegment(sketch, "E1133", {"start": v(13.42, -4.14) * mm, "end": v(13.19, -4.14) * mm});
            skLineSegment(sketch, "E1134", {"start": v(13.19, -4.14) * mm, "end": v(12.96, -4.14) * mm});
            skLineSegment(sketch, "E1135", {"start": v(12.96, -4.14) * mm, "end": v(12.74, -4.14) * mm});
            skLineSegment(sketch, "E1136", {"start": v(12.74, -4.14) * mm, "end": v(12.51, -4.14) * mm});
            skLineSegment(sketch, "E1137", {"start": v(12.51, -4.14) * mm, "end": v(12.28, -4.14) * mm});
            skLineSegment(sketch, "E1138", {"start": v(12.28, -4.14) * mm, "end": v(12.06, -4.14) * mm});
            skLineSegment(sketch, "E1139", {"start": v(12.06, -4.14) * mm, "end": v(11.83, -4.14) * mm});
            skLineSegment(sketch, "E1140", {"start": v(11.83, -4.14) * mm, "end": v(11.6, -4.14) * mm});
            skLineSegment(sketch, "E1141", {"start": v(11.6, -4.14) * mm, "end": v(11.38, -4.14) * mm});
            skLineSegment(sketch, "E1142", {"start": v(11.38, -4.14) * mm, "end": v(11.25, -4.14) * mm});
            skLineSegment(sketch, "E1143", {"start": v(11.25, -4.14) * mm, "end": v(11.12, -4.14) * mm});
            skLineSegment(sketch, "E1144", {"start": v(11.12, -4.14) * mm, "end": v(11, -4.14) * mm});
            skLineSegment(sketch, "E1145", {"start": v(11, -4.14) * mm, "end": v(10.86, -4.14) * mm});
            skLineSegment(sketch, "E1146", {"start": v(10.86, -4.14) * mm, "end": v(10.73, -4.14) * mm});
            skLineSegment(sketch, "E1147", {"start": v(10.73, -4.14) * mm, "end": v(10.6, -4.14) * mm});
            skLineSegment(sketch, "E1148", {"start": v(10.6, -4.14) * mm, "end": v(10.47, -4.14) * mm});
            skLineSegment(sketch, "E1149", {"start": v(10.47, -4.14) * mm, "end": v(10.34, -4.14) * mm});
            skLineSegment(sketch, "E1150", {"start": v(10.34, -4.14) * mm, "end": v(10.22, -4.14) * mm});
            skLineSegment(sketch, "E1151", {"start": v(10.22, -4.14) * mm, "end": v(10.09, -4.14) * mm});
            skLineSegment(sketch, "E1152", {"start": v(10.09, -4.14) * mm, "end": v(9.96, -4.14) * mm});
            skLineSegment(sketch, "E1153", {"start": v(9.96, -4.14) * mm, "end": v(9.83, -4.14) * mm});
            skLineSegment(sketch, "E1154", {"start": v(9.83, -4.14) * mm, "end": v(9.7, -4.14) * mm});
            skLineSegment(sketch, "E1155", {"start": v(9.7, -4.14) * mm, "end": v(9.57, -4.14) * mm});
            skLineSegment(sketch, "E1156", {"start": v(9.57, -4.14) * mm, "end": v(9.44, -4.14) * mm});
            skLineSegment(sketch, "E1157", {"start": v(9.44, -4.14) * mm, "end": v(9.31, -4.14) * mm});
            skLineSegment(sketch, "E1158", {"start": v(-1.03, -1.03) * mm, "end": v(-1.03, -0.9) * mm});
            skLineSegment(sketch, "E1159", {"start": v(-1.03, -0.9) * mm, "end": v(-1.03, -0.78) * mm});
            skLineSegment(sketch, "E1160", {"start": v(-1.03, -0.78) * mm, "end": v(-1.03, -0.65) * mm});
            skLineSegment(sketch, "E1161", {"start": v(-1.03, -0.65) * mm, "end": v(-1.03, -0.52) * mm});
            skLineSegment(sketch, "E1162", {"start": v(-1.03, -0.52) * mm, "end": v(-1.03, -0.39) * mm});
            skLineSegment(sketch, "E1163", {"start": v(-1.03, -0.39) * mm, "end": v(-1.03, -0.26) * mm});
            skLineSegment(sketch, "E1164", {"start": v(-1.03, -0.26) * mm, "end": v(-1.03, -0.13) * mm});
            skLineSegment(sketch, "E1165", {"start": v(-1.03, -0.13) * mm, "end": v(-1.03, 0) * mm});
            skLineSegment(sketch, "E1166", {"start": v(-1.03, 0) * mm, "end": v(-1.03, 0.13) * mm});
            skLineSegment(sketch, "E1167", {"start": v(-1.03, 0.13) * mm, "end": v(-1.03, 0.26) * mm});
            skLineSegment(sketch, "E1168", {"start": v(-1.03, 0.26) * mm, "end": v(-1.03, 0.39) * mm});
            skLineSegment(sketch, "E1169", {"start": v(-1.03, 0.39) * mm, "end": v(-1.03, 0.52) * mm});
            skLineSegment(sketch, "E1170", {"start": v(-1.03, 0.52) * mm, "end": v(-1.03, 0.65) * mm});
            skLineSegment(sketch, "E1171", {"start": v(-1.03, 0.65) * mm, "end": v(-1.03, 0.78) * mm});
            skLineSegment(sketch, "E1172", {"start": v(-1.03, 0.78) * mm, "end": v(-1.03, 0.9) * mm});
            skLineSegment(sketch, "E1173", {"start": v(-1.03, 0.9) * mm, "end": v(-1.03, 1.03) * mm});
            skLineSegment(sketch, "E1174", {"start": v(-1.03, 1.03) * mm, "end": v(-0.9, 1.03) * mm});
            skLineSegment(sketch, "E1175", {"start": v(-0.9, 1.03) * mm, "end": v(-0.78, 1.03) * mm});
            skLineSegment(sketch, "E1176", {"start": v(-0.78, 1.03) * mm, "end": v(-0.65, 1.03) * mm});
            skLineSegment(sketch, "E1177", {"start": v(-0.65, 1.03) * mm, "end": v(-0.52, 1.03) * mm});
            skLineSegment(sketch, "E1178", {"start": v(-0.52, 1.03) * mm, "end": v(-0.39, 1.03) * mm});
            skLineSegment(sketch, "E1179", {"start": v(-0.39, 1.03) * mm, "end": v(-0.26, 1.03) * mm});
            skLineSegment(sketch, "E1180", {"start": v(-0.26, 1.03) * mm, "end": v(-0.13, 1.03) * mm});
            skLineSegment(sketch, "E1181", {"start": v(-0.13, 1.03) * mm, "end": v(0, 1.03) * mm});
            skLineSegment(sketch, "E1182", {"start": v(0, 1.03) * mm, "end": v(0.13, 1.03) * mm});
            skLineSegment(sketch, "E1183", {"start": v(0.13, 1.03) * mm, "end": v(0.26, 1.03) * mm});
            skLineSegment(sketch, "E1184", {"start": v(0.26, 1.03) * mm, "end": v(0.39, 1.03) * mm});
            skLineSegment(sketch, "E1185", {"start": v(0.39, 1.03) * mm, "end": v(0.52, 1.03) * mm});
            skLineSegment(sketch, "E1186", {"start": v(0.52, 1.03) * mm, "end": v(0.65, 1.03) * mm});
            skLineSegment(sketch, "E1187", {"start": v(0.65, 1.03) * mm, "end": v(0.78, 1.03) * mm});
            skLineSegment(sketch, "E1188", {"start": v(0.78, 1.03) * mm, "end": v(0.9, 1.03) * mm});
            skLineSegment(sketch, "E1189", {"start": v(0.9, 1.03) * mm, "end": v(1.03, 1.03) * mm});
            skLineSegment(sketch, "E1190", {"start": v(1.03, 1.03) * mm, "end": v(1.03, 0.9) * mm});
            skLineSegment(sketch, "E1191", {"start": v(1.03, 0.9) * mm, "end": v(1.03, 0.78) * mm});
            skLineSegment(sketch, "E1192", {"start": v(1.03, 0.78) * mm, "end": v(1.03, 0.65) * mm});
            skLineSegment(sketch, "E1193", {"start": v(1.03, 0.65) * mm, "end": v(1.03, 0.52) * mm});
            skLineSegment(sketch, "E1194", {"start": v(1.03, 0.52) * mm, "end": v(1.03, 0.39) * mm});
            skLineSegment(sketch, "E1195", {"start": v(1.03, 0.39) * mm, "end": v(1.03, 0.26) * mm});
            skLineSegment(sketch, "E1196", {"start": v(1.03, 0.26) * mm, "end": v(1.03, 0.13) * mm});
            skLineSegment(sketch, "E1197", {"start": v(1.03, 0.13) * mm, "end": v(1.03, 0) * mm});
            skLineSegment(sketch, "E1198", {"start": v(1.03, 0) * mm, "end": v(1.03, -0.13) * mm});
            skLineSegment(sketch, "E1199", {"start": v(1.03, -0.13) * mm, "end": v(1.03, -0.26) * mm});
            skLineSegment(sketch, "E1200", {"start": v(1.03, -0.26) * mm, "end": v(1.03, -0.39) * mm});
            skLineSegment(sketch, "E1201", {"start": v(1.03, -0.39) * mm, "end": v(1.03, -0.52) * mm});
            skLineSegment(sketch, "E1202", {"start": v(1.03, -0.52) * mm, "end": v(1.03, -0.65) * mm});
            skLineSegment(sketch, "E1203", {"start": v(1.03, -0.65) * mm, "end": v(1.03, -0.78) * mm});
            skLineSegment(sketch, "E1204", {"start": v(1.03, -0.78) * mm, "end": v(1.03, -0.9) * mm});
            skLineSegment(sketch, "E1205", {"start": v(1.03, -0.9) * mm, "end": v(1.03, -1.03) * mm});
            skLineSegment(sketch, "E1206", {"start": v(1.03, -1.03) * mm, "end": v(0.9, -1.03) * mm});
            skLineSegment(sketch, "E1207", {"start": v(0.9, -1.03) * mm, "end": v(0.78, -1.03) * mm});
            skLineSegment(sketch, "E1208", {"start": v(0.78, -1.03) * mm, "end": v(0.65, -1.03) * mm});
            skLineSegment(sketch, "E1209", {"start": v(0.65, -1.03) * mm, "end": v(0.52, -1.03) * mm});
            skLineSegment(sketch, "E1210", {"start": v(0.52, -1.03) * mm, "end": v(0.39, -1.03) * mm});
            skLineSegment(sketch, "E1211", {"start": v(0.39, -1.03) * mm, "end": v(0.26, -1.03) * mm});
            skLineSegment(sketch, "E1212", {"start": v(0.26, -1.03) * mm, "end": v(0.13, -1.03) * mm});
            skLineSegment(sketch, "E1213", {"start": v(0.13, -1.03) * mm, "end": v(0, -1.03) * mm});
            skLineSegment(sketch, "E1214", {"start": v(0, -1.03) * mm, "end": v(-0.13, -1.03) * mm});
            skLineSegment(sketch, "E1215", {"start": v(-0.13, -1.03) * mm, "end": v(-0.26, -1.03) * mm});
            skLineSegment(sketch, "E1216", {"start": v(-0.26, -1.03) * mm, "end": v(-0.39, -1.03) * mm});
            skLineSegment(sketch, "E1217", {"start": v(-0.39, -1.03) * mm, "end": v(-0.52, -1.03) * mm});
            skLineSegment(sketch, "E1218", {"start": v(-0.52, -1.03) * mm, "end": v(-0.65, -1.03) * mm});
            skLineSegment(sketch, "E1219", {"start": v(-0.65, -1.03) * mm, "end": v(-0.78, -1.03) * mm});
            skLineSegment(sketch, "E1220", {"start": v(-0.78, -1.03) * mm, "end": v(-0.9, -1.03) * mm});
            skLineSegment(sketch, "E1221", {"start": v(-0.9, -1.03) * mm, "end": v(-1.03, -1.03) * mm});
            skSolve(sketch);
        }
        {
            var Q0;
            Q0=makeQuery(id+"F3.imprint","IMPRINT",FACE,{"disambiguationData":[TD([[makeQuery(id+"F3.imprint","IMPRINT",EDGE,{"derivedFrom":sQuery(id+"F3.wireOp",EDGE,"E6")}),1.0]])]});
            extrude(context, id + "F4", {"entities" : qUnion([Q0]), "operationType" : NewBodyOperationType.REMOVE, "endBound" : BoundingType.THROUGH_ALL, "oppositeDirection" : true, "depth" : 25 * mm, "offsetDistance" : 25 * mm});
        }
        {
            var Q0;
            Q0=makeQuery(id+"F4.boolean.opBoolean","COPY",FACE,{"derivedFrom":makeQuery(id+"F4.opExtrude","SWEPT_FACE",FACE,{"disambiguationData":[OSD([sQuery(id+"F3.wireOp",EDGE,"E630"),sQuery(id+"F3.wireOp",EDGE,"E631"),sQuery(id+"F3.wireOp",EDGE,"E632"),sQuery(id+"F3.wireOp",EDGE,"E633"),sQuery(id+"F3.wireOp",EDGE,"E634"),sQuery(id+"F3.wireOp",EDGE,"E635"),sQuery(id+"F3.wireOp",EDGE,"E636"),sQuery(id+"F3.wireOp",EDGE,"E637"),sQuery(id+"F3.wireOp",EDGE,"E638"),sQuery(id+"F3.wireOp",EDGE,"E639"),sQuery(id+"F3.wireOp",EDGE,"E640"),sQuery(id+"F3.wireOp",EDGE,"E641"),sQuery(id+"F3.wireOp",EDGE,"E642"),sQuery(id+"F3.wireOp",EDGE,"E643"),sQuery(id+"F3.wireOp",EDGE,"E644"),sQuery(id+"F3.wireOp",EDGE,"E645"),sQuery(id+"F3.wireOp",EDGE,"E646"),sQuery(id+"F3.wireOp",EDGE,"E647"),sQuery(id+"F3.wireOp",EDGE,"E648"),sQuery(id+"F3.wireOp",EDGE,"E649"),sQuery(id+"F3.wireOp",EDGE,"E650"),sQuery(id+"F3.wireOp",EDGE,"E651"),sQuery(id+"F3.wireOp",EDGE,"E652"),sQuery(id+"F3.wireOp",EDGE,"E653"),sQuery(id+"F3.wireOp",EDGE,"E654"),sQuery(id+"F3.wireOp",EDGE,"E655"),sQuery(id+"F3.wireOp",EDGE,"E656"),sQuery(id+"F3.wireOp",EDGE,"E657"),sQuery(id+"F3.wireOp",EDGE,"E658"),sQuery(id+"F3.wireOp",EDGE,"E659"),sQuery(id+"F3.wireOp",EDGE,"E660"),sQuery(id+"F3.wireOp",EDGE,"E661")])]})});
            var sketch = newSketch(context, id + "F5", { "sketchPlane" : qUnion([Q0])});
            skLineSegment(sketch, "E1222.bottom", {"start": v(-1.03, 0) * mm, "end": v(1.03, 0) * mm});
            skLineSegment(sketch, "E1222.top", {"start": v(-1.03, 2) * mm, "end": v(1.03, 2) * mm});
            skLineSegment(sketch, "E1222.left", {"start": v(-1.03, 0) * mm, "end": v(-1.03, 2) * mm});
            skLineSegment(sketch, "E1222.right", {"start": v(1.03, 0) * mm, "end": v(1.03, 2) * mm});
            skSolve(sketch);
        }
        {
            var Q0;
            Q0 = qSketchRegion(id + "F5", true);
            extrude(context, id + "F6", {"entities" : qUnion([Q0]), "operationType" : NewBodyOperationType.ADD, "endBound" : BoundingType.UP_TO_NEXT, "depth" : 25 * mm, "offsetDistance" : 25 * mm});
        }
        {
            var Q0;
            Q0=qCreatedBy(makeId("Front.planeOp"),FACE);
            var sketch = newSketch(context, id + "F7", { "sketchPlane" : qUnion([Q0])});
            skLineSegment(sketch, "E1223", {"start": v(0, 0) * mm, "end": v(0, 5.05) * mm, "construction": true});
            skSolve(sketch);
        }
        {
            var Q0;
            Q0=qCreatedBy(makeId("Front.planeOp"),FACE);
            var sketch = newSketch(context, id + "F8", { "sketchPlane" : qUnion([Q0])});
            skCircle(sketch, "E1224", {"center": v(-15, 5) * mm, "radius": 4 * mm});
            skLineSegment(sketch, "E1225", {"start": v(-17.93, 2.28) * mm, "end": v(-15.82, 0) * mm});
            skLineSegment(sketch, "E1226", {"start": v(-16.82, 0) * mm, "end": v(-18.21, 1.17) * mm, "construction": true});
            skLineSegment(sketch, "E1227", {"start": v(-11.94, 2.43) * mm, "end": v(-13.97, 0) * mm});
            skLineSegment(sketch, "E1228", {"start": v(-15.82, 0) * mm, "end": v(-13.97, 0) * mm});
            skSolve(sketch);
        }
        {
            var Q0;
            Q0 = qSketchRegion(id + "F8", true);
            var Q1;
            Q1=sQuery(id+"F0.wireOp",EDGE,"E3");
            revolve(context, id + "F9", {"operationType" : NewBodyOperationType.ADD, "surfaceOperationType" : NewSurfaceOperationType.NEW, "entities" : qUnion([Q0]), "axis" : qUnion([Q1]), "revolveType" : RevolveType.FULL});
        }
        {
            var Q0;
            Q0=qCreatedBy(makeId("Top.planeOp"),FACE);
            var sketch = newSketch(context, id + "F10", { "sketchPlane" : qUnion([Q0])});
            skCircle(sketch, "E1229", {"center": v(0, 21) * mm, "radius": 4 * mm});
            skSolve(sketch);
        }
        {
            var Q0;
            Q0=makeQuery(id+"F10.imprint","IMPRINT",FACE,{"disambiguationData":[TD([[makeQuery(id+"F10.imprint","IMPRINT",EDGE,{"derivedFrom":sQuery(id+"F10.wireOp",EDGE,"E1229")}),1.0]])]});
            extrude(context, id + "F11", {"entities" : qUnion([Q0]), "operationType" : NewBodyOperationType.REMOVE, "depth" : 25 * mm, "offsetDistance" : 25 * mm});
        }
        {
            var Q0;
            Q0=makeQuery(id+"F11.boolean.opBoolean","INTERSECT",EDGE,{"derivedFrom":[makeQuery(id+"F4.boolean.opBoolean","SPLIT",FACE,{"disambiguationData":[TD([makeQuery(id+"F1.opRevolve","SWEPT_FACE",FACE,{"disambiguationData":[OSD([sQuery(id+"F0.wireOp",EDGE,"E2")])]}),makeQuery(id+"F4.opExtrude","SWEPT_FACE",FACE,{"disambiguationData":[OSD([sQuery(id+"F3.wireOp",EDGE,"705da5c4-06c6-4740-92ce-35b712dfc936.0")])]}),makeQuery(id+"F4.opExtrude","SWEPT_FACE",FACE,{"disambiguationData":[OSD([sQuery(id+"F3.wireOp",EDGE,"705da5c4-06c6-4740-92ce-35b712dfc936.1")])]}),makeQuery(id+"F4.opExtrude","SWEPT_FACE",FACE,{"disambiguationData":[OSD([sQuery(id+"F3.wireOp",EDGE,"705da5c4-06c6-4740-92ce-35b712dfc936.2")])]}),makeQuery(id+"F4.opExtrude","SWEPT_FACE",FACE,{"disambiguationData":[OSD([sQuery(id+"F3.wireOp",EDGE,"705da5c4-06c6-4740-92ce-35b712dfc936.3")])]}),makeQuery(id+"F4.opExtrude","SWEPT_FACE",FACE,{"disambiguationData":[OSD([sQuery(id+"F3.wireOp",EDGE,"705da5c4-06c6-4740-92ce-35b712dfc936.4")])]}),makeQuery(id+"F4.opExtrude","SWEPT_FACE",FACE,{"disambiguationData":[OSD([sQuery(id+"F3.wireOp",EDGE,"705da5c4-06c6-4740-92ce-35b712dfc936.5")])]})])],"derivedFrom":makeQuery(id+"F1.opRevolve","SWEPT_FACE",FACE,{"disambiguationData":[OSD([sQuery(id+"F0.wireOp",EDGE,"E1")])]})}),makeQuery(id+"F11.opExtrude","SWEPT_FACE",FACE,{"disambiguationData":[OSD([sQuery(id+"F10.wireOp",EDGE,"E1229")])]})]});
            fillet(context, id + "F12", {"entities" : qUnion([Q0]), "radius" : 1 * mm, "tangentPropagation" : true, "allowEdgeOverflow" : false});
        }
    });
